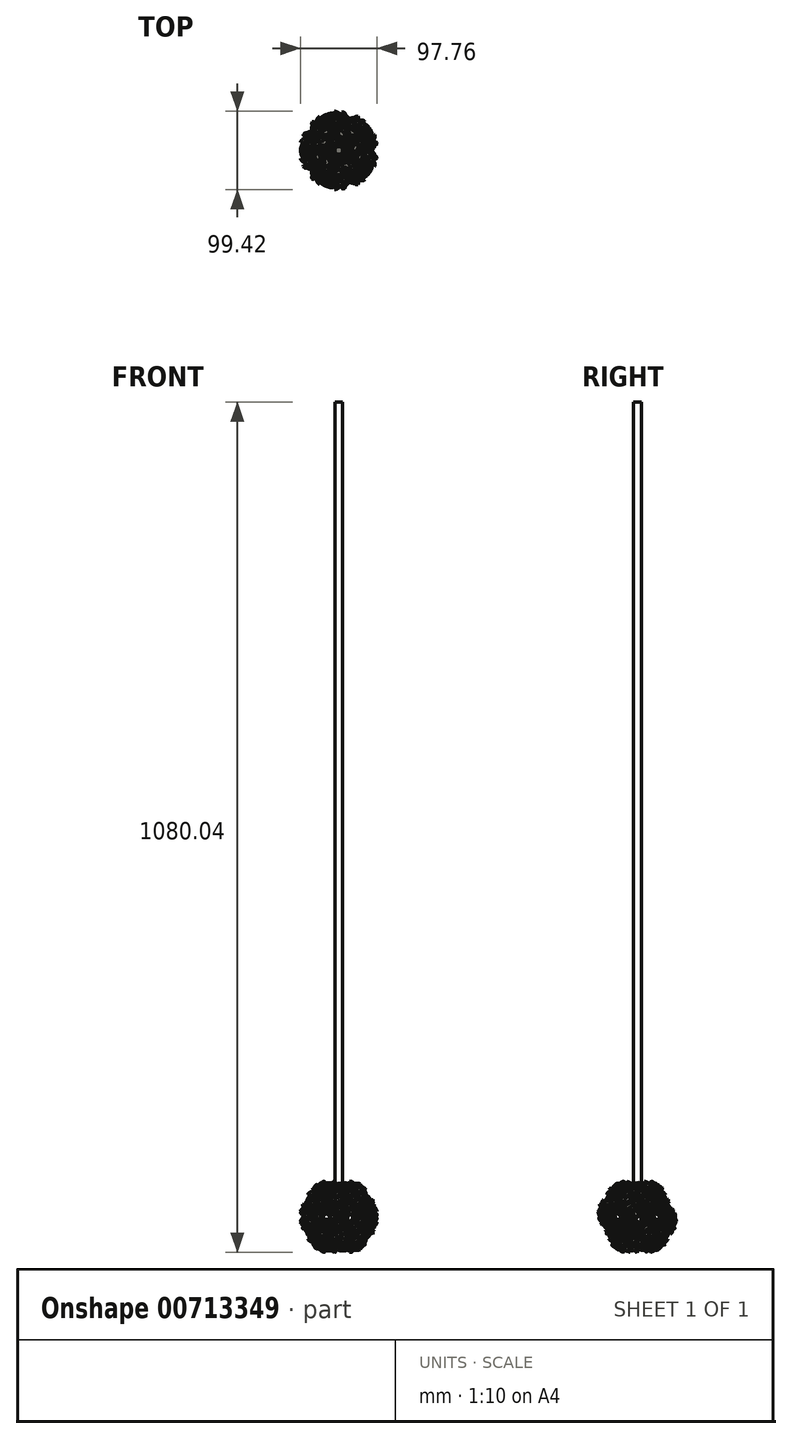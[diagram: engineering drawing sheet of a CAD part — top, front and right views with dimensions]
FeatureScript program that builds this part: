
annotation { "Feature Type Name" : "Feature", "Feature Type Description" : "" }
export const myFeature = defineFeature(function(context is Context, id is Id, definition is map)
    precondition{}
    {
        {
            var Q0;
            Q0=qCreatedBy(makeId("Top.planeOp"),FACE);
            var sketch = newSketch(context, id + "F0", { "sketchPlane" : qUnion([Q0])});
            skCircle(sketch, "E0.cCircle", {"center": v(0, 0) * mm, "radius": 10.32 * mm, "construction": true});
            skLineSegment(sketch, "E0.0", {"start": v(7.5, -10.32) * mm, "end": v(-7.5, -10.32) * mm});
            skLineSegment(sketch, "E0.1", {"start": v(-7.5, -10.32) * mm, "end": v(-12.14, 3.94) * mm});
            skLineSegment(sketch, "E0.2", {"start": v(-12.14, 3.94) * mm, "end": v(0, 12.76) * mm});
            skLineSegment(sketch, "E0.3", {"start": v(0, 12.76) * mm, "end": v(12.14, 3.94) * mm});
            skLineSegment(sketch, "E0.4", {"start": v(12.14, 3.94) * mm, "end": v(7.5, -10.32) * mm});
            skPoint(sketch, "E0.0.midPoint", {"position": v(0, -10.32) * mm});
            skLineSegment(sketch, "E1", {"start": v(0, 12.76) * mm, "end": v(0, -10.32) * mm});
            skSolve(sketch);
        }
        {
            var Q0;
            Q0=qCreatedBy(makeId("Top.planeOp"),FACE);
            var sketch = newSketch(context, id + "F1", { "sketchPlane" : qUnion([Q0])});
            skCircle(sketch, "E2.cCircle", {"center": v(22.17, -7.2) * mm, "radius": 13 * mm, "construction": true});
            skLineSegment(sketch, "E2.0", {"start": v(36.84, -4.09) * mm, "end": v(32.2, -18.35) * mm});
            skLineSegment(sketch, "E2.1", {"start": v(32.2, -18.35) * mm, "end": v(17.54, -21.47) * mm});
            skLineSegment(sketch, "E2.2", {"start": v(17.54, -21.47) * mm, "end": v(7.5, -10.32) * mm});
            skLineSegment(sketch, "E2.3", {"start": v(7.5, -10.32) * mm, "end": v(12.14, 3.94) * mm});
            skLineSegment(sketch, "E2.4", {"start": v(12.14, 3.94) * mm, "end": v(26.8, 7.06) * mm});
            skLineSegment(sketch, "E2.5", {"start": v(26.8, 7.06) * mm, "end": v(36.84, -4.09) * mm});
            skPoint(sketch, "E2.0.midPoint", {"position": v(34.53, -11.22) * mm});
            skSolve(sketch);
        }
        {
            var Q0;
            Q0=makeQuery(id+"F0.imprint","IMPRINT",FACE,{"disambiguationData":[TD([[makeQuery(id+"F0.imprint","IMPRINT",EDGE,{"derivedFrom":sQuery(id+"F0.wireOp",EDGE,"E0.0")}),-1.0]])]});
            extrude(context, id + "F2", {"entities" : qUnion([Q0]), "oppositeDirection" : true, "depth" : 1 * mm});
        }
        {
            var Q0;
            Q0=makeQuery(id+"F1.imprint","IMPRINT",FACE,{"disambiguationData":[TD([[makeQuery(id+"F1.imprint","IMPRINT",EDGE,{"derivedFrom":sQuery(id+"F1.wireOp",EDGE,"E2.0")}),-1.0]])]});
            extrude(context, id + "F3", {"entities" : qUnion([Q0]), "oppositeDirection" : true, "depth" : 1 * mm});
        }
        {
            var Q0;
            Q0=makeQuery(id+"F3.opExtrude","SWEPT_BODY",BODY,{"disambiguationData":[OSD([sQuery(id+"F1.wireOp",EDGE,"E2.0"),sQuery(id+"F1.wireOp",EDGE,"E2.1"),sQuery(id+"F1.wireOp",EDGE,"E2.2"),sQuery(id+"F1.wireOp",EDGE,"E2.3"),sQuery(id+"F1.wireOp",EDGE,"E2.4"),sQuery(id+"F1.wireOp",EDGE,"E2.5")])]});
            var Q1;
            Q1=makeQuery(id+"F2.opExtrude","CAP_EDGE",EDGE,{"disambiguationData":[OSD([sQuery(id+"F0.wireOp",EDGE,"E0.4")])],"isStart":true});
            transform(context, id + "F4", {"entities" : qUnion([Q0]), "transformType" : TransformType.ROTATION, "transformAxis" : qUnion([Q1]), "angle" : 37.38 * degree, "oppositeDirection" : true, "makeCopy" : false});
        }
        {
            var Q0;
            Q0=qCreatedBy(makeId("Right.planeOp"),FACE);
            var sketch = newSketch(context, id + "F5", { "sketchPlane" : qUnion([Q0])});
            skLineSegment(sketch, "E3", {"start": v(0, 0) * mm, "end": v(0, 7.73) * mm});
            skSolve(sketch);
        }
        {
            var Q0;
            Q0=makeQuery(id+"F3.opExtrude","SWEPT_BODY",BODY,{"disambiguationData":[OSD([sQuery(id+"F1.wireOp",EDGE,"E2.0"),sQuery(id+"F1.wireOp",EDGE,"E2.1"),sQuery(id+"F1.wireOp",EDGE,"E2.2"),sQuery(id+"F1.wireOp",EDGE,"E2.3"),sQuery(id+"F1.wireOp",EDGE,"E2.4"),sQuery(id+"F1.wireOp",EDGE,"E2.5")])]});
            var Q1;
            Q1=sQuery(id+"F5.wireOp",EDGE,"E3");
            circularPattern(context, id + "F6", {"entities" : qUnion([Q0]), "axis" : qUnion([Q1]), "angle" : 72 * degree, "instanceCount" : round(5)});
        }
        {
            var Q0;
            Q0=makeQuery(id+"F6.opPattern","COPY",FACE,{"derivedFrom":makeQuery(id+"F3.opExtrude","CAP_FACE",FACE,{"disambiguationData":[OSD([sQuery(id+"F1.wireOp",EDGE,"E2.0"),sQuery(id+"F1.wireOp",EDGE,"E2.1"),sQuery(id+"F1.wireOp",EDGE,"E2.2"),sQuery(id+"F1.wireOp",EDGE,"E2.3"),sQuery(id+"F1.wireOp",EDGE,"E2.4"),sQuery(id+"F1.wireOp",EDGE,"E2.5")])],"isStart":true}),"instanceName":"4"});
            var sketch = newSketch(context, id + "F7", { "sketchPlane" : qUnion([Q0])});
            skLineSegment(sketch, "E4", {"start": v(0, -34.18) * mm, "end": v(0, -8.2) * mm});
            skLineSegment(sketch, "E5", {"start": v(-15, -21.2) * mm, "end": v(15, -21.2) * mm});
            skCircle(sketch, "E6", {"center": v(0, -21.2) * mm, "radius": 3.24 * mm});
            skSolve(sketch);
        }
        {
            var Q0;
            Q0=qCreatedBy(makeId("Right.planeOp"),FACE);
            var sketch = newSketch(context, id + "F8", { "sketchPlane" : qUnion([Q0])});
            skArc(sketch, "E7.0", {"start": v(-1.37, 0) * mm, "mid": v(-18.04, 14.75) * mm, "end": v(-20.04, -7.42) * mm});
            skLineSegment(sketch, "E8", {"start": v(-20.04, -7.42) * mm, "end": v(-24.47, -10.8) * mm});
            skLineSegment(sketch, "E9", {"start": v(-1.37, 0) * mm, "end": v(0, 0) * mm});
            skArc(sketch, "E10", {"start": v(1.07, 1.27) * mm, "mid": v(3.46, 7.37) * mm, "end": v(2.5, 13.85) * mm});
            skArc(sketch, "E11", {"start": v(-0.8, 8.97) * mm, "mid": v(1.84, 10.74) * mm, "end": v(2.5, 13.85) * mm});
            skArc(sketch, "E12.1.0", {"start": v(-0.8, 8.97) * mm, "mid": v(-2.13, 15.94) * mm, "end": v(-6.98, 21.1) * mm});
            skArc(sketch, "E12.1.1", {"start": v(-6.75, 15.32) * mm, "mid": v(-5.72, 18.26) * mm, "end": v(-6.98, 21.1) * mm});
            skArc(sketch, "E12.2.0", {"start": v(-6.75, 15.32) * mm, "mid": v(-11.92, 20.18) * mm, "end": v(-18.89, 21.5) * mm});
            skArc(sketch, "E12.2.1", {"start": v(-15.3, 16.96) * mm, "mid": v(-16.2, 19.94) * mm, "end": v(-18.89, 21.5) * mm});
            skArc(sketch, "E12.3.0", {"start": v(-15.3, 16.96) * mm, "mid": v(-22.34, 17.85) * mm, "end": v(-28.75, 14.83) * mm});
            skArc(sketch, "E12.3.1", {"start": v(-23.18, 13.26) * mm, "mid": v(-25.66, 15.15) * mm, "end": v(-28.75, 14.83) * mm});
            skArc(sketch, "E12.4.0", {"start": v(-23.18, 13.26) * mm, "mid": v(-29.4, 9.84) * mm, "end": v(-32.81, 3.63) * mm});
            skArc(sketch, "E12.4.1", {"start": v(-27.38, 5.64) * mm, "mid": v(-30.5, 5.7) * mm, "end": v(-32.81, 3.63) * mm});
            skArc(sketch, "E12.5.0", {"start": v(-27.38, 5.64) * mm, "mid": v(-30.4, -0.78) * mm, "end": v(-29.51, -7.81) * mm});
            skArc(sketch, "E12.5.1", {"start": v(-26.3, -3) * mm, "mid": v(-28.86, -4.77) * mm, "end": v(-29.51, -7.81) * mm});
            skArc(sketch, "E12.6.0", {"start": v(-26.3, -3) * mm, "mid": v(-26.03, -7.06) * mm, "end": v(-24.49, -10.82) * mm});
            skArc(sketch, "E13", {"start": v(-24.49, -10.82) * mm, "mid": v(-20.56, -11.35) * mm, "end": v(-20.04, -7.42) * mm});
            skArc(sketch, "E14", {"start": v(-1.37, 0) * mm, "mid": v(1.27, -2.11) * mm, "end": v(1.07, 1.27) * mm});
            skSolve(sketch);
        }
        {
            var Q0;
            {var subQ2=sQuery(id+"F8.wireOp",EDGE,"E7.0");Q0=makeQuery(id+"F8.imprint","IMPRINT",FACE,{"disambiguationData":[TD([[makeQuery(id+"F8.imprint","IMPRINT",EDGE,{"derivedFrom":subQ2}),-1.0]])]});}
            extrude(context, id + "F9", {"entities" : qUnion([Q0]), "oppositeDirection" : true, "depth" : 2 * mm});
        }
        {
            var Q0;
            Q0=makeQuery(id+"F9.opExtrude","SWEPT_EDGE",EDGE,{"disambiguationData":[OSD([sQuery(id+"F8.wireOp",EDGE,"E10"),sQuery(id+"F8.wireOp",EDGE,"E14")])]});
            fillet(context, id + "F10", {"entities" : qUnion([Q0]), "radius" : 5 * mm, "tangentPropagation" : true, "allowEdgeOverflow" : false});
        }
        {
            var Q0;
            Q0=qCreatedBy(makeId("Right.planeOp"),FACE);
            var sketch = newSketch(context, id + "F11", { "sketchPlane" : qUnion([Q0])});
            skLineSegment(sketch, "E15", {"start": v(0, 0) * mm, "end": v(-20.65, -7.89) * mm});
            skLineSegment(sketch, "E16", {"start": v(0, 0) * mm, "end": v(0, 28.42) * mm});
            skSolve(sketch);
        }
        {
            var Q0;
            Q0=makeQuery(id+"F9.opExtrude","SWEPT_BODY",BODY,{"disambiguationData":[OSD([sQuery(id+"F8.wireOp",EDGE,"003f2e54-bd62-4f0b-a98e-8c36e71e2cf6"),sQuery(id+"F8.wireOp",EDGE,"8c729305-40a1-49fa-b790-4b99a3909bb6"),sQuery(id+"F8.wireOp",EDGE,"862a2a8f-3db7-4421-9c69-6ab2f53c4c24.1.0"),sQuery(id+"F8.wireOp",EDGE,"862a2a8f-3db7-4421-9c69-6ab2f53c4c24.1.1"),sQuery(id+"F8.wireOp",EDGE,"862a2a8f-3db7-4421-9c69-6ab2f53c4c24.2.0"),sQuery(id+"F8.wireOp",EDGE,"862a2a8f-3db7-4421-9c69-6ab2f53c4c24.2.1"),sQuery(id+"F8.wireOp",EDGE,"862a2a8f-3db7-4421-9c69-6ab2f53c4c24.3.0"),sQuery(id+"F8.wireOp",EDGE,"862a2a8f-3db7-4421-9c69-6ab2f53c4c24.3.1"),sQuery(id+"F8.wireOp",EDGE,"862a2a8f-3db7-4421-9c69-6ab2f53c4c24.4.0"),sQuery(id+"F8.wireOp",EDGE,"862a2a8f-3db7-4421-9c69-6ab2f53c4c24.4.1"),sQuery(id+"F8.wireOp",EDGE,"862a2a8f-3db7-4421-9c69-6ab2f53c4c24.5.0"),sQuery(id+"F8.wireOp",EDGE,"E7.0"),sQuery(id+"F8.wireOp",EDGE,"E8"),sQuery(id+"F8.wireOp",EDGE,"E9")])]});
            var Q1;
            Q1=sQuery(id+"F11.wireOp",EDGE,"E15");
            transform(context, id + "F12", {"entities" : qUnion([Q0]), "transformType" : TransformType.ROTATION, "transformAxis" : qUnion([Q1]), "angle" : 65 * degree, "makeCopy" : false});
        }
        {
            var Q0;
            Q0=makeQuery(id+"F9.opExtrude","SWEPT_BODY",BODY,{"disambiguationData":[OSD([sQuery(id+"F8.wireOp",EDGE,"003f2e54-bd62-4f0b-a98e-8c36e71e2cf6"),sQuery(id+"F8.wireOp",EDGE,"8c729305-40a1-49fa-b790-4b99a3909bb6"),sQuery(id+"F8.wireOp",EDGE,"862a2a8f-3db7-4421-9c69-6ab2f53c4c24.1.0"),sQuery(id+"F8.wireOp",EDGE,"862a2a8f-3db7-4421-9c69-6ab2f53c4c24.1.1"),sQuery(id+"F8.wireOp",EDGE,"862a2a8f-3db7-4421-9c69-6ab2f53c4c24.2.0"),sQuery(id+"F8.wireOp",EDGE,"862a2a8f-3db7-4421-9c69-6ab2f53c4c24.2.1"),sQuery(id+"F8.wireOp",EDGE,"862a2a8f-3db7-4421-9c69-6ab2f53c4c24.3.0"),sQuery(id+"F8.wireOp",EDGE,"862a2a8f-3db7-4421-9c69-6ab2f53c4c24.3.1"),sQuery(id+"F8.wireOp",EDGE,"862a2a8f-3db7-4421-9c69-6ab2f53c4c24.4.0"),sQuery(id+"F8.wireOp",EDGE,"862a2a8f-3db7-4421-9c69-6ab2f53c4c24.4.1"),sQuery(id+"F8.wireOp",EDGE,"862a2a8f-3db7-4421-9c69-6ab2f53c4c24.5.0"),sQuery(id+"F8.wireOp",EDGE,"E7.0"),sQuery(id+"F8.wireOp",EDGE,"E8"),sQuery(id+"F8.wireOp",EDGE,"E9")])]});
            var Q1;
            Q1=sQuery(id+"F11.wireOp",EDGE,"E16");
            circularPattern(context, id + "F13", {"entities" : qUnion([Q0]), "axis" : qUnion([Q1]), "angle" : 72 * degree, "instanceCount" : round(5)});
        }
        {
            var Q0;
            Q0=qCreatedBy(makeId("Right.planeOp"),FACE);
            var sketch = newSketch(context, id + "F14", { "sketchPlane" : qUnion([Q0])});
            skLineSegment(sketch, "E17.0", {"start": v(-30.97, -15.77) * mm, "end": v(-10.32, 0) * mm});
            skLineSegment(sketch, "E18", {"start": v(-20.65, -7.89) * mm, "end": v(-30.05, 4.42) * mm});
            skSolve(sketch);
        }
        {
            var Q0;
            Q0=makeQuery(id+"F9.opExtrude","SWEPT_BODY",BODY,{"disambiguationData":[OSD([sQuery(id+"F8.wireOp",EDGE,"003f2e54-bd62-4f0b-a98e-8c36e71e2cf6"),sQuery(id+"F8.wireOp",EDGE,"8c729305-40a1-49fa-b790-4b99a3909bb6"),sQuery(id+"F8.wireOp",EDGE,"862a2a8f-3db7-4421-9c69-6ab2f53c4c24.1.0"),sQuery(id+"F8.wireOp",EDGE,"862a2a8f-3db7-4421-9c69-6ab2f53c4c24.1.1"),sQuery(id+"F8.wireOp",EDGE,"862a2a8f-3db7-4421-9c69-6ab2f53c4c24.2.0"),sQuery(id+"F8.wireOp",EDGE,"862a2a8f-3db7-4421-9c69-6ab2f53c4c24.2.1"),sQuery(id+"F8.wireOp",EDGE,"862a2a8f-3db7-4421-9c69-6ab2f53c4c24.3.0"),sQuery(id+"F8.wireOp",EDGE,"862a2a8f-3db7-4421-9c69-6ab2f53c4c24.3.1"),sQuery(id+"F8.wireOp",EDGE,"862a2a8f-3db7-4421-9c69-6ab2f53c4c24.4.0"),sQuery(id+"F8.wireOp",EDGE,"862a2a8f-3db7-4421-9c69-6ab2f53c4c24.4.1"),sQuery(id+"F8.wireOp",EDGE,"862a2a8f-3db7-4421-9c69-6ab2f53c4c24.5.0"),sQuery(id+"F8.wireOp",EDGE,"E7.0"),sQuery(id+"F8.wireOp",EDGE,"E8"),sQuery(id+"F8.wireOp",EDGE,"E9")])]});
            var Q1;
            Q1=sQuery(id+"F14.wireOp",EDGE,"E18");
            circularPattern(context, id + "F15", {"entities" : qUnion([Q0]), "axis" : qUnion([Q1]), "angle" : 120 * degree, "instanceCount" : round(3)});
        }
        {
            var Q0;
            Q0=makeQuery(id+"F15.opPattern","COPY",BODY,{"derivedFrom":makeQuery(id+"F9.opExtrude","SWEPT_BODY",BODY,{"disambiguationData":[OSD([sQuery(id+"F8.wireOp",EDGE,"E7.0"),sQuery(id+"F8.wireOp",EDGE,"E10"),sQuery(id+"F8.wireOp",EDGE,"E11"),sQuery(id+"F8.wireOp",EDGE,"E12.1.0"),sQuery(id+"F8.wireOp",EDGE,"E12.1.1"),sQuery(id+"F8.wireOp",EDGE,"E12.2.0"),sQuery(id+"F8.wireOp",EDGE,"E12.2.1"),sQuery(id+"F8.wireOp",EDGE,"E12.3.0"),sQuery(id+"F8.wireOp",EDGE,"E12.3.1"),sQuery(id+"F8.wireOp",EDGE,"E12.4.0"),sQuery(id+"F8.wireOp",EDGE,"E12.4.1"),sQuery(id+"F8.wireOp",EDGE,"E12.5.0"),sQuery(id+"F8.wireOp",EDGE,"E12.5.1"),sQuery(id+"F8.wireOp",EDGE,"E12.6.0"),sQuery(id+"F8.wireOp",EDGE,"E13"),sQuery(id+"F8.wireOp",EDGE,"E14")])]}),"instanceName":"2"});
            var Q1;
            Q1=makeQuery(id+"F15.opPattern","COPY",BODY,{"derivedFrom":makeQuery(id+"F9.opExtrude","SWEPT_BODY",BODY,{"disambiguationData":[OSD([sQuery(id+"F8.wireOp",EDGE,"E7.0"),sQuery(id+"F8.wireOp",EDGE,"E10"),sQuery(id+"F8.wireOp",EDGE,"E11"),sQuery(id+"F8.wireOp",EDGE,"E12.1.0"),sQuery(id+"F8.wireOp",EDGE,"E12.1.1"),sQuery(id+"F8.wireOp",EDGE,"E12.2.0"),sQuery(id+"F8.wireOp",EDGE,"E12.2.1"),sQuery(id+"F8.wireOp",EDGE,"E12.3.0"),sQuery(id+"F8.wireOp",EDGE,"E12.3.1"),sQuery(id+"F8.wireOp",EDGE,"E12.4.0"),sQuery(id+"F8.wireOp",EDGE,"E12.4.1"),sQuery(id+"F8.wireOp",EDGE,"E12.5.0"),sQuery(id+"F8.wireOp",EDGE,"E12.5.1"),sQuery(id+"F8.wireOp",EDGE,"E12.6.0"),sQuery(id+"F8.wireOp",EDGE,"E13"),sQuery(id+"F8.wireOp",EDGE,"E14")])]}),"instanceName":"1"});
            var Q2;
            Q2=sQuery(id+"F11.wireOp",EDGE,"E16");
            circularPattern(context, id + "F16", {"entities" : qUnion([Q0, Q1]), "axis" : qUnion([Q2]), "angle" : 72 * degree, "instanceCount" : round(5)});
        }
        {
            var Q0;
            Q0=makeQuery(id+"F3.opExtrude","SWEPT_BODY",BODY,{"disambiguationData":[OSD([sQuery(id+"F1.wireOp",EDGE,"E2.0"),sQuery(id+"F1.wireOp",EDGE,"E2.1"),sQuery(id+"F1.wireOp",EDGE,"E2.2"),sQuery(id+"F1.wireOp",EDGE,"E2.3"),sQuery(id+"F1.wireOp",EDGE,"E2.4"),sQuery(id+"F1.wireOp",EDGE,"E2.5")])]});
            var Q1;
            Q1=makeQuery(id+"F16.opPattern","COPY",BODY,{"derivedFrom":makeQuery(id+"F15.opPattern","COPY",BODY,{"derivedFrom":makeQuery(id+"F9.opExtrude","SWEPT_BODY",BODY,{"disambiguationData":[OSD([sQuery(id+"F8.wireOp",EDGE,"E7.0"),sQuery(id+"F8.wireOp",EDGE,"E10"),sQuery(id+"F8.wireOp",EDGE,"E11"),sQuery(id+"F8.wireOp",EDGE,"E12.1.0"),sQuery(id+"F8.wireOp",EDGE,"E12.1.1"),sQuery(id+"F8.wireOp",EDGE,"E12.2.0"),sQuery(id+"F8.wireOp",EDGE,"E12.2.1"),sQuery(id+"F8.wireOp",EDGE,"E12.3.0"),sQuery(id+"F8.wireOp",EDGE,"E12.3.1"),sQuery(id+"F8.wireOp",EDGE,"E12.4.0"),sQuery(id+"F8.wireOp",EDGE,"E12.4.1"),sQuery(id+"F8.wireOp",EDGE,"E12.5.0"),sQuery(id+"F8.wireOp",EDGE,"E12.5.1"),sQuery(id+"F8.wireOp",EDGE,"E12.6.0"),sQuery(id+"F8.wireOp",EDGE,"E13"),sQuery(id+"F8.wireOp",EDGE,"E14")])]}),"instanceName":"1"}),"instanceName":"1"});
            var Q2;
            Q2=makeQuery(id+"F13.opPattern","COPY",BODY,{"derivedFrom":makeQuery(id+"F9.opExtrude","SWEPT_BODY",BODY,{"disambiguationData":[OSD([sQuery(id+"F8.wireOp",EDGE,"E7.0"),sQuery(id+"F8.wireOp",EDGE,"E10"),sQuery(id+"F8.wireOp",EDGE,"E11"),sQuery(id+"F8.wireOp",EDGE,"E12.1.0"),sQuery(id+"F8.wireOp",EDGE,"E12.1.1"),sQuery(id+"F8.wireOp",EDGE,"E12.2.0"),sQuery(id+"F8.wireOp",EDGE,"E12.2.1"),sQuery(id+"F8.wireOp",EDGE,"E12.3.0"),sQuery(id+"F8.wireOp",EDGE,"E12.3.1"),sQuery(id+"F8.wireOp",EDGE,"E12.4.0"),sQuery(id+"F8.wireOp",EDGE,"E12.4.1"),sQuery(id+"F8.wireOp",EDGE,"E12.5.0"),sQuery(id+"F8.wireOp",EDGE,"E12.5.1"),sQuery(id+"F8.wireOp",EDGE,"E12.6.0"),sQuery(id+"F8.wireOp",EDGE,"E13"),sQuery(id+"F8.wireOp",EDGE,"E14")])]}),"instanceName":"1"});
            var Q3;
            Q3=makeQuery(id+"F16.opPattern","COPY",BODY,{"derivedFrom":makeQuery(id+"F15.opPattern","COPY",BODY,{"derivedFrom":makeQuery(id+"F9.opExtrude","SWEPT_BODY",BODY,{"disambiguationData":[OSD([sQuery(id+"F8.wireOp",EDGE,"E7.0"),sQuery(id+"F8.wireOp",EDGE,"E10"),sQuery(id+"F8.wireOp",EDGE,"E11"),sQuery(id+"F8.wireOp",EDGE,"E12.1.0"),sQuery(id+"F8.wireOp",EDGE,"E12.1.1"),sQuery(id+"F8.wireOp",EDGE,"E12.2.0"),sQuery(id+"F8.wireOp",EDGE,"E12.2.1"),sQuery(id+"F8.wireOp",EDGE,"E12.3.0"),sQuery(id+"F8.wireOp",EDGE,"E12.3.1"),sQuery(id+"F8.wireOp",EDGE,"E12.4.0"),sQuery(id+"F8.wireOp",EDGE,"E12.4.1"),sQuery(id+"F8.wireOp",EDGE,"E12.5.0"),sQuery(id+"F8.wireOp",EDGE,"E12.5.1"),sQuery(id+"F8.wireOp",EDGE,"E12.6.0"),sQuery(id+"F8.wireOp",EDGE,"E13"),sQuery(id+"F8.wireOp",EDGE,"E14")])]}),"instanceName":"2"}),"instanceName":"1"});
            var Q4;
            Q4=sQuery(id+"F14.wireOp",EDGE,"E18");
            circularPattern(context, id + "F17", {"entities" : qUnion([Q0, Q1, Q2, Q3]), "axis" : qUnion([Q4]), "angle" : 120 * degree, "instanceCount" : 2, "oppositeDirection" : true});
        }
        {
            var Q0;
            Q0=makeQuery(id+"F2.opExtrude","SWEPT_BODY",BODY,{"disambiguationData":[OSD([sQuery(id+"F0.wireOp",EDGE,"E0.0"),sQuery(id+"F0.wireOp",EDGE,"E0.1"),sQuery(id+"F0.wireOp",EDGE,"E0.2"),sQuery(id+"F0.wireOp",EDGE,"E0.3"),sQuery(id+"F0.wireOp",EDGE,"E0.4")])]});
            var Q1;
            Q1=makeQuery(id+"F13.opPattern","COPY",BODY,{"derivedFrom":makeQuery(id+"F9.opExtrude","SWEPT_BODY",BODY,{"disambiguationData":[OSD([sQuery(id+"F8.wireOp",EDGE,"E7.0"),sQuery(id+"F8.wireOp",EDGE,"E10"),sQuery(id+"F8.wireOp",EDGE,"E11"),sQuery(id+"F8.wireOp",EDGE,"E12.1.0"),sQuery(id+"F8.wireOp",EDGE,"E12.1.1"),sQuery(id+"F8.wireOp",EDGE,"E12.2.0"),sQuery(id+"F8.wireOp",EDGE,"E12.2.1"),sQuery(id+"F8.wireOp",EDGE,"E12.3.0"),sQuery(id+"F8.wireOp",EDGE,"E12.3.1"),sQuery(id+"F8.wireOp",EDGE,"E12.4.0"),sQuery(id+"F8.wireOp",EDGE,"E12.4.1"),sQuery(id+"F8.wireOp",EDGE,"E12.5.0"),sQuery(id+"F8.wireOp",EDGE,"E12.5.1"),sQuery(id+"F8.wireOp",EDGE,"E12.6.0"),sQuery(id+"F8.wireOp",EDGE,"E13"),sQuery(id+"F8.wireOp",EDGE,"E14")])]}),"instanceName":"2"});
            var Q2;
            Q2=makeQuery(id+"F13.opPattern","COPY",BODY,{"derivedFrom":makeQuery(id+"F9.opExtrude","SWEPT_BODY",BODY,{"disambiguationData":[OSD([sQuery(id+"F8.wireOp",EDGE,"E7.0"),sQuery(id+"F8.wireOp",EDGE,"E10"),sQuery(id+"F8.wireOp",EDGE,"E11"),sQuery(id+"F8.wireOp",EDGE,"E12.1.0"),sQuery(id+"F8.wireOp",EDGE,"E12.1.1"),sQuery(id+"F8.wireOp",EDGE,"E12.2.0"),sQuery(id+"F8.wireOp",EDGE,"E12.2.1"),sQuery(id+"F8.wireOp",EDGE,"E12.3.0"),sQuery(id+"F8.wireOp",EDGE,"E12.3.1"),sQuery(id+"F8.wireOp",EDGE,"E12.4.0"),sQuery(id+"F8.wireOp",EDGE,"E12.4.1"),sQuery(id+"F8.wireOp",EDGE,"E12.5.0"),sQuery(id+"F8.wireOp",EDGE,"E12.5.1"),sQuery(id+"F8.wireOp",EDGE,"E12.6.0"),sQuery(id+"F8.wireOp",EDGE,"E13"),sQuery(id+"F8.wireOp",EDGE,"E14")])]}),"instanceName":"3"});
            var Q3;
            Q3=sQuery(id+"F14.wireOp",EDGE,"E18");
            circularPattern(context, id + "F18", {"entities" : qUnion([Q0, Q1, Q2]), "axis" : qUnion([Q3]), "angle" : 120 * degree, "instanceCount" : round(3)});
        }
        {
            var Q0;
            Q0=makeQuery(id+"F18.opPattern","COPY",FACE,{"derivedFrom":makeQuery(id+"F2.opExtrude","CAP_FACE",FACE,{"disambiguationData":[OSD([sQuery(id+"F0.wireOp",EDGE,"E0.0"),sQuery(id+"F0.wireOp",EDGE,"E0.1"),sQuery(id+"F0.wireOp",EDGE,"E0.2"),sQuery(id+"F0.wireOp",EDGE,"E0.3"),sQuery(id+"F0.wireOp",EDGE,"E0.4")])],"isStart":true}),"instanceName":"1"});
            var sketch = newSketch(context, id + "F19", { "sketchPlane" : qUnion([Q0])});
            skLineSegment(sketch, "E19", {"start": v(-1.3, -23.63) * mm, "end": v(-19.97, -37.2) * mm});
            skLineSegment(sketch, "E20", {"start": v(-19.97, -22.2) * mm, "end": v(-1.3, -35.77) * mm});
            skSolve(sketch);
        }
        {
            var Q0;
            Q0=sQuery(id+"F19.wireOp",VERTEX,"E19.end");
            var Q1;
            Q1=sQuery(id+"F19.wireOp",VERTEX,"E19.start");
            var Q2;
            Q2=sQuery(id+"F14.wireOp",VERTEX,"E18.end");
            cPlane(context, id + "F20", {"entities" : qUnion([Q0, Q1, Q2]), "cplaneType" : CPlaneType.THREE_POINT, "offset" : 150 * mm, "width" : 150 * mm, "height" : 150 * mm});
        }
        {
            var Q0;
            Q0=qCreatedBy(id+"F20.planeOp",FACE);
            var sketch = newSketch(context, id + "F21", { "sketchPlane" : qUnion([Q0])});
            skLineSegment(sketch, "E21.0", {"start": v(23.59, 6.27) * mm, "end": v(41.93, -7.75) * mm});
            skLineSegment(sketch, "E21.1", {"start": v(34.92, -2.4) * mm, "end": v(29.26, 1.94) * mm});
            skLineSegment(sketch, "E22", {"start": v(31.8, 0) * mm, "end": v(33.22, 1.87) * mm});
            skLineSegment(sketch, "E23", {"start": v(33.22, 1.87) * mm, "end": v(37.58, 7.58) * mm});
            skSolve(sketch);
        }
        {
            var Q0;
            Q0=makeQuery(id+"F17.opPattern","COPY",BODY,{"derivedFrom":makeQuery(id+"F3.opExtrude","SWEPT_BODY",BODY,{"disambiguationData":[OSD([sQuery(id+"F1.wireOp",EDGE,"E2.0"),sQuery(id+"F1.wireOp",EDGE,"E2.1"),sQuery(id+"F1.wireOp",EDGE,"E2.2"),sQuery(id+"F1.wireOp",EDGE,"E2.3"),sQuery(id+"F1.wireOp",EDGE,"E2.4"),sQuery(id+"F1.wireOp",EDGE,"E2.5")])]}),"instanceName":"1"});
            var Q1;
            Q1=makeQuery(id+"F17.opPattern","COPY",BODY,{"derivedFrom":makeQuery(id+"F13.opPattern","COPY",BODY,{"derivedFrom":makeQuery(id+"F9.opExtrude","SWEPT_BODY",BODY,{"disambiguationData":[OSD([sQuery(id+"F8.wireOp",EDGE,"E7.0"),sQuery(id+"F8.wireOp",EDGE,"E10"),sQuery(id+"F8.wireOp",EDGE,"E11"),sQuery(id+"F8.wireOp",EDGE,"E12.1.0"),sQuery(id+"F8.wireOp",EDGE,"E12.1.1"),sQuery(id+"F8.wireOp",EDGE,"E12.2.0"),sQuery(id+"F8.wireOp",EDGE,"E12.2.1"),sQuery(id+"F8.wireOp",EDGE,"E12.3.0"),sQuery(id+"F8.wireOp",EDGE,"E12.3.1"),sQuery(id+"F8.wireOp",EDGE,"E12.4.0"),sQuery(id+"F8.wireOp",EDGE,"E12.4.1"),sQuery(id+"F8.wireOp",EDGE,"E12.5.0"),sQuery(id+"F8.wireOp",EDGE,"E12.5.1"),sQuery(id+"F8.wireOp",EDGE,"E12.6.0"),sQuery(id+"F8.wireOp",EDGE,"E13"),sQuery(id+"F8.wireOp",EDGE,"E14")])]}),"instanceName":"1"}),"instanceName":"1"});
            var Q2;
            Q2=makeQuery(id+"F17.opPattern","COPY",BODY,{"derivedFrom":makeQuery(id+"F16.opPattern","COPY",BODY,{"derivedFrom":makeQuery(id+"F15.opPattern","COPY",BODY,{"derivedFrom":makeQuery(id+"F9.opExtrude","SWEPT_BODY",BODY,{"disambiguationData":[OSD([sQuery(id+"F8.wireOp",EDGE,"E7.0"),sQuery(id+"F8.wireOp",EDGE,"E10"),sQuery(id+"F8.wireOp",EDGE,"E11"),sQuery(id+"F8.wireOp",EDGE,"E12.1.0"),sQuery(id+"F8.wireOp",EDGE,"E12.1.1"),sQuery(id+"F8.wireOp",EDGE,"E12.2.0"),sQuery(id+"F8.wireOp",EDGE,"E12.2.1"),sQuery(id+"F8.wireOp",EDGE,"E12.3.0"),sQuery(id+"F8.wireOp",EDGE,"E12.3.1"),sQuery(id+"F8.wireOp",EDGE,"E12.4.0"),sQuery(id+"F8.wireOp",EDGE,"E12.4.1"),sQuery(id+"F8.wireOp",EDGE,"E12.5.0"),sQuery(id+"F8.wireOp",EDGE,"E12.5.1"),sQuery(id+"F8.wireOp",EDGE,"E12.6.0"),sQuery(id+"F8.wireOp",EDGE,"E13"),sQuery(id+"F8.wireOp",EDGE,"E14")])]}),"instanceName":"2"}),"instanceName":"1"}),"instanceName":"1"});
            var Q3;
            Q3=makeQuery(id+"F17.opPattern","COPY",BODY,{"derivedFrom":makeQuery(id+"F16.opPattern","COPY",BODY,{"derivedFrom":makeQuery(id+"F15.opPattern","COPY",BODY,{"derivedFrom":makeQuery(id+"F9.opExtrude","SWEPT_BODY",BODY,{"disambiguationData":[OSD([sQuery(id+"F8.wireOp",EDGE,"E7.0"),sQuery(id+"F8.wireOp",EDGE,"E10"),sQuery(id+"F8.wireOp",EDGE,"E11"),sQuery(id+"F8.wireOp",EDGE,"E12.1.0"),sQuery(id+"F8.wireOp",EDGE,"E12.1.1"),sQuery(id+"F8.wireOp",EDGE,"E12.2.0"),sQuery(id+"F8.wireOp",EDGE,"E12.2.1"),sQuery(id+"F8.wireOp",EDGE,"E12.3.0"),sQuery(id+"F8.wireOp",EDGE,"E12.3.1"),sQuery(id+"F8.wireOp",EDGE,"E12.4.0"),sQuery(id+"F8.wireOp",EDGE,"E12.4.1"),sQuery(id+"F8.wireOp",EDGE,"E12.5.0"),sQuery(id+"F8.wireOp",EDGE,"E12.5.1"),sQuery(id+"F8.wireOp",EDGE,"E12.6.0"),sQuery(id+"F8.wireOp",EDGE,"E13"),sQuery(id+"F8.wireOp",EDGE,"E14")])]}),"instanceName":"1"}),"instanceName":"1"}),"instanceName":"1"});
            var Q4;
            Q4=sQuery(id+"F21.wireOp",EDGE,"E22");
            circularPattern(context, id + "F22", {"entities" : qUnion([Q0, Q1, Q2, Q3]), "axis" : qUnion([Q4]), "angle" : 72 * degree, "instanceCount" : round(3), "oppositeDirection" : true});
        }
        {
            var Q0;
            Q0=makeQuery(id+"F18.opPattern","COPY",FACE,{"derivedFrom":makeQuery(id+"F2.opExtrude","CAP_FACE",FACE,{"disambiguationData":[OSD([sQuery(id+"F0.wireOp",EDGE,"E0.0"),sQuery(id+"F0.wireOp",EDGE,"E0.1"),sQuery(id+"F0.wireOp",EDGE,"E0.2"),sQuery(id+"F0.wireOp",EDGE,"E0.3"),sQuery(id+"F0.wireOp",EDGE,"E0.4")])],"isStart":true}),"instanceName":"2"});
            var sketch = newSketch(context, id + "F23", { "sketchPlane" : qUnion([Q0])});
            skLineSegment(sketch, "E24", {"start": v(1.3, -23.63) * mm, "end": v(19.97, -37.2) * mm});
            skLineSegment(sketch, "E25", {"start": v(5.7, -41.83) * mm, "end": v(12.84, -19.88) * mm});
            skSolve(sketch);
        }
        {
            var Q0;
            Q0=sQuery(id+"F23.wireOp",VERTEX,"E24.end");
            var Q1;
            Q1=sQuery(id+"F23.wireOp",VERTEX,"E24.start");
            var Q2;
            Q2=sQuery(id+"F14.wireOp",VERTEX,"E18.end");
            cPlane(context, id + "F24", {"entities" : qUnion([Q0, Q1, Q2]), "cplaneType" : CPlaneType.THREE_POINT, "offset" : 150 * mm, "width" : 150 * mm, "height" : 150 * mm});
        }
        {
            var Q0;
            Q0=qCreatedBy(id+"F24.planeOp",FACE);
            var sketch = newSketch(context, id + "F25", { "sketchPlane" : qUnion([Q0])});
            skLineSegment(sketch, "E26.0", {"start": v(23.59, 6.27) * mm, "end": v(41.93, -7.75) * mm});
            skLineSegment(sketch, "E26.1", {"start": v(34.92, -2.4) * mm, "end": v(29.26, 1.94) * mm});
            skLineSegment(sketch, "E27", {"start": v(31.8, 0) * mm, "end": v(36.23, 5.8) * mm});
            skSolve(sketch);
        }
        {
            var Q0;
            Q0=makeQuery(id+"F3.opExtrude","SWEPT_BODY",BODY,{"disambiguationData":[OSD([sQuery(id+"F1.wireOp",EDGE,"E2.0"),sQuery(id+"F1.wireOp",EDGE,"E2.1"),sQuery(id+"F1.wireOp",EDGE,"E2.2"),sQuery(id+"F1.wireOp",EDGE,"E2.3"),sQuery(id+"F1.wireOp",EDGE,"E2.4"),sQuery(id+"F1.wireOp",EDGE,"E2.5")])]});
            var Q1;
            Q1=makeQuery(id+"F16.opPattern","COPY",BODY,{"derivedFrom":makeQuery(id+"F15.opPattern","COPY",BODY,{"derivedFrom":makeQuery(id+"F9.opExtrude","SWEPT_BODY",BODY,{"disambiguationData":[OSD([sQuery(id+"F8.wireOp",EDGE,"E7.0"),sQuery(id+"F8.wireOp",EDGE,"E10"),sQuery(id+"F8.wireOp",EDGE,"E11"),sQuery(id+"F8.wireOp",EDGE,"E12.1.0"),sQuery(id+"F8.wireOp",EDGE,"E12.1.1"),sQuery(id+"F8.wireOp",EDGE,"E12.2.0"),sQuery(id+"F8.wireOp",EDGE,"E12.2.1"),sQuery(id+"F8.wireOp",EDGE,"E12.3.0"),sQuery(id+"F8.wireOp",EDGE,"E12.3.1"),sQuery(id+"F8.wireOp",EDGE,"E12.4.0"),sQuery(id+"F8.wireOp",EDGE,"E12.4.1"),sQuery(id+"F8.wireOp",EDGE,"E12.5.0"),sQuery(id+"F8.wireOp",EDGE,"E12.5.1"),sQuery(id+"F8.wireOp",EDGE,"E12.6.0"),sQuery(id+"F8.wireOp",EDGE,"E13"),sQuery(id+"F8.wireOp",EDGE,"E14")])]}),"instanceName":"2"}),"instanceName":"1"});
            var Q2;
            Q2=makeQuery(id+"F13.opPattern","COPY",BODY,{"derivedFrom":makeQuery(id+"F9.opExtrude","SWEPT_BODY",BODY,{"disambiguationData":[OSD([sQuery(id+"F8.wireOp",EDGE,"E7.0"),sQuery(id+"F8.wireOp",EDGE,"E10"),sQuery(id+"F8.wireOp",EDGE,"E11"),sQuery(id+"F8.wireOp",EDGE,"E12.1.0"),sQuery(id+"F8.wireOp",EDGE,"E12.1.1"),sQuery(id+"F8.wireOp",EDGE,"E12.2.0"),sQuery(id+"F8.wireOp",EDGE,"E12.2.1"),sQuery(id+"F8.wireOp",EDGE,"E12.3.0"),sQuery(id+"F8.wireOp",EDGE,"E12.3.1"),sQuery(id+"F8.wireOp",EDGE,"E12.4.0"),sQuery(id+"F8.wireOp",EDGE,"E12.4.1"),sQuery(id+"F8.wireOp",EDGE,"E12.5.0"),sQuery(id+"F8.wireOp",EDGE,"E12.5.1"),sQuery(id+"F8.wireOp",EDGE,"E12.6.0"),sQuery(id+"F8.wireOp",EDGE,"E13"),sQuery(id+"F8.wireOp",EDGE,"E14")])]}),"instanceName":"1"});
            var Q3;
            Q3=makeQuery(id+"F16.opPattern","COPY",BODY,{"derivedFrom":makeQuery(id+"F15.opPattern","COPY",BODY,{"derivedFrom":makeQuery(id+"F9.opExtrude","SWEPT_BODY",BODY,{"disambiguationData":[OSD([sQuery(id+"F8.wireOp",EDGE,"E7.0"),sQuery(id+"F8.wireOp",EDGE,"E10"),sQuery(id+"F8.wireOp",EDGE,"E11"),sQuery(id+"F8.wireOp",EDGE,"E12.1.0"),sQuery(id+"F8.wireOp",EDGE,"E12.1.1"),sQuery(id+"F8.wireOp",EDGE,"E12.2.0"),sQuery(id+"F8.wireOp",EDGE,"E12.2.1"),sQuery(id+"F8.wireOp",EDGE,"E12.3.0"),sQuery(id+"F8.wireOp",EDGE,"E12.3.1"),sQuery(id+"F8.wireOp",EDGE,"E12.4.0"),sQuery(id+"F8.wireOp",EDGE,"E12.4.1"),sQuery(id+"F8.wireOp",EDGE,"E12.5.0"),sQuery(id+"F8.wireOp",EDGE,"E12.5.1"),sQuery(id+"F8.wireOp",EDGE,"E12.6.0"),sQuery(id+"F8.wireOp",EDGE,"E13"),sQuery(id+"F8.wireOp",EDGE,"E14")])]}),"instanceName":"1"}),"instanceName":"1"});
            var Q4;
            Q4=sQuery(id+"F25.wireOp",EDGE,"E27");
            circularPattern(context, id + "F26", {"entities" : qUnion([Q0, Q1, Q2, Q3]), "axis" : qUnion([Q4]), "angle" : 72 * degree, "instanceCount" : round(3), "oppositeDirection" : true});
        }
        {
            var Q0;
            Q0=makeQuery(id+"F17.opPattern","COPY",FACE,{"derivedFrom":makeQuery(id+"F3.opExtrude","CAP_FACE",FACE,{"disambiguationData":[OSD([sQuery(id+"F1.wireOp",EDGE,"E2.0"),sQuery(id+"F1.wireOp",EDGE,"E2.1"),sQuery(id+"F1.wireOp",EDGE,"E2.2"),sQuery(id+"F1.wireOp",EDGE,"E2.3"),sQuery(id+"F1.wireOp",EDGE,"E2.4"),sQuery(id+"F1.wireOp",EDGE,"E2.5")])],"isStart":true}),"instanceName":"1"});
            var sketch = newSketch(context, id + "F27", { "sketchPlane" : qUnion([Q0])});
            skLineSegment(sketch, "E28", {"start": v(0, -47.28) * mm, "end": v(0, -21.3) * mm});
            skSolve(sketch);
        }
        {
            var Q0;
            Q0=qCreatedBy(makeId("Right.planeOp"),FACE);
            var sketch = newSketch(context, id + "F28", { "sketchPlane" : qUnion([Q0])});
            skLineSegment(sketch, "E29.0", {"start": v(-35.84, -41.3) * mm, "end": v(-30.97, -15.77) * mm});
            skLineSegment(sketch, "E30", {"start": v(-33.4, -28.53) * mm, "end": v(-47.6, -25.82) * mm});
            skSolve(sketch);
        }
        {
            var Q0;
            Q0=makeQuery(id+"F18.opPattern","COPY",BODY,{"derivedFrom":makeQuery(id+"F2.opExtrude","SWEPT_BODY",BODY,{"disambiguationData":[OSD([sQuery(id+"F0.wireOp",EDGE,"E0.0"),sQuery(id+"F0.wireOp",EDGE,"E0.1"),sQuery(id+"F0.wireOp",EDGE,"E0.2"),sQuery(id+"F0.wireOp",EDGE,"E0.3"),sQuery(id+"F0.wireOp",EDGE,"E0.4")])]}),"instanceName":"2"});
            var Q1;
            Q1=sQuery(id+"F28.wireOp",EDGE,"E30");
            circularPattern(context, id + "F29", {"entities" : qUnion([Q0]), "axis" : qUnion([Q1]), "angle" : 120 * degree, "instanceCount" : 2, "oppositeDirection" : true});
        }
        {
            var Q0;
            Q0=makeQuery(id+"F29.opPattern","COPY",FACE,{"derivedFrom":makeQuery(id+"F18.opPattern","COPY",FACE,{"derivedFrom":makeQuery(id+"F2.opExtrude","CAP_FACE",FACE,{"disambiguationData":[OSD([sQuery(id+"F0.wireOp",EDGE,"E0.0"),sQuery(id+"F0.wireOp",EDGE,"E0.1"),sQuery(id+"F0.wireOp",EDGE,"E0.2"),sQuery(id+"F0.wireOp",EDGE,"E0.3"),sQuery(id+"F0.wireOp",EDGE,"E0.4")])],"isStart":true}),"instanceName":"2"}),"instanceName":"1"});
            var sketch = newSketch(context, id + "F30", { "sketchPlane" : qUnion([Q0])});
            skLineSegment(sketch, "E31", {"start": v(0, -43.99) * mm, "end": v(0, -31.23) * mm});
            skLineSegment(sketch, "E32", {"start": v(-12.14, -35.17) * mm, "end": v(9.82, -28.04) * mm});
            skPoint(sketch, "E33.orphan", {"position": v(0, -20.9) * mm});
            skSolve(sketch);
        }
        {
            var Q0;
            Q0=qCreatedBy(makeId("Right.planeOp"),FACE);
            var sketch = newSketch(context, id + "F31", { "sketchPlane" : qUnion([Q0])});
            skLineSegment(sketch, "E34.0", {"start": v(-25.52, -61.94) * mm, "end": v(-31.23, -50.52) * mm});
            skLineSegment(sketch, "E35", {"start": v(-31.23, -50.52) * mm, "end": v(-51.07, -60.45) * mm});
            skSolve(sketch);
        }
        {
            var Q0;
            Q0=makeQuery(id+"F26.opPattern","COPY",BODY,{"derivedFrom":makeQuery(id+"F3.opExtrude","SWEPT_BODY",BODY,{"disambiguationData":[OSD([sQuery(id+"F1.wireOp",EDGE,"E2.0"),sQuery(id+"F1.wireOp",EDGE,"E2.1"),sQuery(id+"F1.wireOp",EDGE,"E2.2"),sQuery(id+"F1.wireOp",EDGE,"E2.3"),sQuery(id+"F1.wireOp",EDGE,"E2.4"),sQuery(id+"F1.wireOp",EDGE,"E2.5")])]}),"instanceName":"2"});
            var Q1;
            Q1=makeQuery(id+"F26.opPattern","COPY",BODY,{"derivedFrom":makeQuery(id+"F16.opPattern","COPY",BODY,{"derivedFrom":makeQuery(id+"F15.opPattern","COPY",BODY,{"derivedFrom":makeQuery(id+"F9.opExtrude","SWEPT_BODY",BODY,{"disambiguationData":[OSD([sQuery(id+"F8.wireOp",EDGE,"E7.0"),sQuery(id+"F8.wireOp",EDGE,"E10"),sQuery(id+"F8.wireOp",EDGE,"E11"),sQuery(id+"F8.wireOp",EDGE,"E12.1.0"),sQuery(id+"F8.wireOp",EDGE,"E12.1.1"),sQuery(id+"F8.wireOp",EDGE,"E12.2.0"),sQuery(id+"F8.wireOp",EDGE,"E12.2.1"),sQuery(id+"F8.wireOp",EDGE,"E12.3.0"),sQuery(id+"F8.wireOp",EDGE,"E12.3.1"),sQuery(id+"F8.wireOp",EDGE,"E12.4.0"),sQuery(id+"F8.wireOp",EDGE,"E12.4.1"),sQuery(id+"F8.wireOp",EDGE,"E12.5.0"),sQuery(id+"F8.wireOp",EDGE,"E12.5.1"),sQuery(id+"F8.wireOp",EDGE,"E12.6.0"),sQuery(id+"F8.wireOp",EDGE,"E13"),sQuery(id+"F8.wireOp",EDGE,"E14")])]}),"instanceName":"2"}),"instanceName":"1"}),"instanceName":"2"});
            var Q2;
            Q2=makeQuery(id+"F26.opPattern","COPY",BODY,{"derivedFrom":makeQuery(id+"F13.opPattern","COPY",BODY,{"derivedFrom":makeQuery(id+"F9.opExtrude","SWEPT_BODY",BODY,{"disambiguationData":[OSD([sQuery(id+"F8.wireOp",EDGE,"E7.0"),sQuery(id+"F8.wireOp",EDGE,"E10"),sQuery(id+"F8.wireOp",EDGE,"E11"),sQuery(id+"F8.wireOp",EDGE,"E12.1.0"),sQuery(id+"F8.wireOp",EDGE,"E12.1.1"),sQuery(id+"F8.wireOp",EDGE,"E12.2.0"),sQuery(id+"F8.wireOp",EDGE,"E12.2.1"),sQuery(id+"F8.wireOp",EDGE,"E12.3.0"),sQuery(id+"F8.wireOp",EDGE,"E12.3.1"),sQuery(id+"F8.wireOp",EDGE,"E12.4.0"),sQuery(id+"F8.wireOp",EDGE,"E12.4.1"),sQuery(id+"F8.wireOp",EDGE,"E12.5.0"),sQuery(id+"F8.wireOp",EDGE,"E12.5.1"),sQuery(id+"F8.wireOp",EDGE,"E12.6.0"),sQuery(id+"F8.wireOp",EDGE,"E13"),sQuery(id+"F8.wireOp",EDGE,"E14")])]}),"instanceName":"1"}),"instanceName":"2"});
            var Q3;
            Q3=makeQuery(id+"F18.opPattern","COPY",BODY,{"derivedFrom":makeQuery(id+"F13.opPattern","COPY",BODY,{"derivedFrom":makeQuery(id+"F9.opExtrude","SWEPT_BODY",BODY,{"disambiguationData":[OSD([sQuery(id+"F8.wireOp",EDGE,"E7.0"),sQuery(id+"F8.wireOp",EDGE,"E10"),sQuery(id+"F8.wireOp",EDGE,"E11"),sQuery(id+"F8.wireOp",EDGE,"E12.1.0"),sQuery(id+"F8.wireOp",EDGE,"E12.1.1"),sQuery(id+"F8.wireOp",EDGE,"E12.2.0"),sQuery(id+"F8.wireOp",EDGE,"E12.2.1"),sQuery(id+"F8.wireOp",EDGE,"E12.3.0"),sQuery(id+"F8.wireOp",EDGE,"E12.3.1"),sQuery(id+"F8.wireOp",EDGE,"E12.4.0"),sQuery(id+"F8.wireOp",EDGE,"E12.4.1"),sQuery(id+"F8.wireOp",EDGE,"E12.5.0"),sQuery(id+"F8.wireOp",EDGE,"E12.5.1"),sQuery(id+"F8.wireOp",EDGE,"E12.6.0"),sQuery(id+"F8.wireOp",EDGE,"E13"),sQuery(id+"F8.wireOp",EDGE,"E14")])]}),"instanceName":"2"}),"instanceName":"2"});
            var Q4;
            Q4=sQuery(id+"F31.wireOp",EDGE,"E35");
            circularPattern(context, id + "F32", {"entities" : qUnion([Q0, Q1, Q2, Q3]), "axis" : qUnion([Q4]), "angle" : 72 * degree, "instanceCount" : round(3), "oppositeDirection" : true});
        }
        {
            var Q0;
            Q0=makeQuery(id+"F6.opPattern","COPY",FACE,{"derivedFrom":makeQuery(id+"F3.opExtrude","CAP_FACE",FACE,{"disambiguationData":[OSD([sQuery(id+"F1.wireOp",EDGE,"E2.0"),sQuery(id+"F1.wireOp",EDGE,"E2.1"),sQuery(id+"F1.wireOp",EDGE,"E2.2"),sQuery(id+"F1.wireOp",EDGE,"E2.3"),sQuery(id+"F1.wireOp",EDGE,"E2.4"),sQuery(id+"F1.wireOp",EDGE,"E2.5")])],"isStart":true}),"instanceName":"2"});
            var sketch = newSketch(context, id + "F33", { "sketchPlane" : qUnion([Q0])});
            skLineSegment(sketch, "E36", {"start": v(-4.1, 7.1) * mm, "end": v(-17.1, 29.6) * mm});
            skSolve(sketch);
        }
        {
            var Q0;
            Q0=sQuery(id+"F33.wireOp",VERTEX,"E36.end");
            var Q1;
            Q1=sQuery(id+"F33.wireOp",VERTEX,"E36.start");
            var Q2;
            Q2=sQuery(id+"F11.wireOp",VERTEX,"E16.end");
            cPlane(context, id + "F34", {"entities" : qUnion([Q0, Q1, Q2]), "cplaneType" : CPlaneType.THREE_POINT, "offset" : 150 * mm, "width" : 150 * mm, "height" : 150 * mm});
        }
        {
            var Q0;
            Q0=qCreatedBy(id+"F34.planeOp",FACE);
            var sketch = newSketch(context, id + "F35", { "sketchPlane" : qUnion([Q0])});
            skLineSegment(sketch, "E37.0", {"start": v(10.32, 0) * mm, "end": v(30.97, -15.77) * mm});
            skLineSegment(sketch, "E38", {"start": v(20.65, -7.89) * mm, "end": v(38.57, 15.58) * mm});
            skSolve(sketch);
        }
        {
            var Q0;
            Q0=makeQuery(id+"F2.opExtrude","SWEPT_BODY",BODY,{"disambiguationData":[OSD([sQuery(id+"F0.wireOp",EDGE,"E0.0"),sQuery(id+"F0.wireOp",EDGE,"E0.1"),sQuery(id+"F0.wireOp",EDGE,"E0.2"),sQuery(id+"F0.wireOp",EDGE,"E0.3"),sQuery(id+"F0.wireOp",EDGE,"E0.4")])]});
            var Q1;
            Q1=sQuery(id+"F35.wireOp",EDGE,"E38");
            circularPattern(context, id + "F36", {"entities" : qUnion([Q0]), "axis" : qUnion([Q1]), "angle" : 120 * degree, "instanceCount" : round(3), "oppositeDirection" : true});
        }
        {
            var Q0;
            Q0=makeQuery(id+"F36.opPattern","COPY",FACE,{"derivedFrom":makeQuery(id+"F2.opExtrude","CAP_FACE",FACE,{"disambiguationData":[OSD([sQuery(id+"F0.wireOp",EDGE,"E0.0"),sQuery(id+"F0.wireOp",EDGE,"E0.1"),sQuery(id+"F0.wireOp",EDGE,"E0.2"),sQuery(id+"F0.wireOp",EDGE,"E0.3"),sQuery(id+"F0.wireOp",EDGE,"E0.4")])],"isStart":true}),"instanceName":"1"});
            var sketch = newSketch(context, id + "F37", { "sketchPlane" : qUnion([Q0])});
            skLineSegment(sketch, "E39", {"start": v(-4.5, -30.9) * mm, "end": v(1.45, -42.2) * mm});
            skPoint(sketch, "E40.orphan", {"position": v(-9.3, -21.76) * mm});
            skSolve(sketch);
        }
        {
            var Q0;
            Q0=sQuery(id+"F37.wireOp",VERTEX,"E39.end");
            var Q1;
            Q1=sQuery(id+"F37.wireOp",VERTEX,"E39.start");
            var Q2;
            Q2=sQuery(id+"F35.wireOp",VERTEX,"E38.end");
            cPlane(context, id + "F38", {"entities" : qUnion([Q0, Q1, Q2]), "cplaneType" : CPlaneType.THREE_POINT, "offset" : 150 * mm, "width" : 150 * mm, "height" : 150 * mm});
        }
        {
            var Q0;
            Q0=qCreatedBy(id+"F38.planeOp",FACE);
            var sketch = newSketch(context, id + "F39", { "sketchPlane" : qUnion([Q0])});
            skLineSegment(sketch, "E41.0", {"start": v(29.7, -11.34) * mm, "end": v(36.4, -22.2) * mm});
            skLineSegment(sketch, "E42", {"start": v(29.7, -11.34) * mm, "end": v(58.3, 6.33) * mm});
            skSolve(sketch);
        }
        {
            var Q0;
            Q0=makeQuery(id+"F22.opPattern","COPY",BODY,{"derivedFrom":makeQuery(id+"F17.opPattern","COPY",BODY,{"derivedFrom":makeQuery(id+"F3.opExtrude","SWEPT_BODY",BODY,{"disambiguationData":[OSD([sQuery(id+"F1.wireOp",EDGE,"E2.0"),sQuery(id+"F1.wireOp",EDGE,"E2.1"),sQuery(id+"F1.wireOp",EDGE,"E2.2"),sQuery(id+"F1.wireOp",EDGE,"E2.3"),sQuery(id+"F1.wireOp",EDGE,"E2.4"),sQuery(id+"F1.wireOp",EDGE,"E2.5")])]}),"instanceName":"1"}),"instanceName":"2"});
            var Q1;
            Q1=makeQuery(id+"F22.opPattern","COPY",BODY,{"derivedFrom":makeQuery(id+"F17.opPattern","COPY",BODY,{"derivedFrom":makeQuery(id+"F16.opPattern","COPY",BODY,{"derivedFrom":makeQuery(id+"F15.opPattern","COPY",BODY,{"derivedFrom":makeQuery(id+"F9.opExtrude","SWEPT_BODY",BODY,{"disambiguationData":[OSD([sQuery(id+"F8.wireOp",EDGE,"E7.0"),sQuery(id+"F8.wireOp",EDGE,"E10"),sQuery(id+"F8.wireOp",EDGE,"E11"),sQuery(id+"F8.wireOp",EDGE,"E12.1.0"),sQuery(id+"F8.wireOp",EDGE,"E12.1.1"),sQuery(id+"F8.wireOp",EDGE,"E12.2.0"),sQuery(id+"F8.wireOp",EDGE,"E12.2.1"),sQuery(id+"F8.wireOp",EDGE,"E12.3.0"),sQuery(id+"F8.wireOp",EDGE,"E12.3.1"),sQuery(id+"F8.wireOp",EDGE,"E12.4.0"),sQuery(id+"F8.wireOp",EDGE,"E12.4.1"),sQuery(id+"F8.wireOp",EDGE,"E12.5.0"),sQuery(id+"F8.wireOp",EDGE,"E12.5.1"),sQuery(id+"F8.wireOp",EDGE,"E12.6.0"),sQuery(id+"F8.wireOp",EDGE,"E13"),sQuery(id+"F8.wireOp",EDGE,"E14")])]}),"instanceName":"2"}),"instanceName":"1"}),"instanceName":"1"}),"instanceName":"2"});
            var Q2;
            Q2=makeQuery(id+"F22.opPattern","COPY",BODY,{"derivedFrom":makeQuery(id+"F17.opPattern","COPY",BODY,{"derivedFrom":makeQuery(id+"F13.opPattern","COPY",BODY,{"derivedFrom":makeQuery(id+"F9.opExtrude","SWEPT_BODY",BODY,{"disambiguationData":[OSD([sQuery(id+"F8.wireOp",EDGE,"E7.0"),sQuery(id+"F8.wireOp",EDGE,"E10"),sQuery(id+"F8.wireOp",EDGE,"E11"),sQuery(id+"F8.wireOp",EDGE,"E12.1.0"),sQuery(id+"F8.wireOp",EDGE,"E12.1.1"),sQuery(id+"F8.wireOp",EDGE,"E12.2.0"),sQuery(id+"F8.wireOp",EDGE,"E12.2.1"),sQuery(id+"F8.wireOp",EDGE,"E12.3.0"),sQuery(id+"F8.wireOp",EDGE,"E12.3.1"),sQuery(id+"F8.wireOp",EDGE,"E12.4.0"),sQuery(id+"F8.wireOp",EDGE,"E12.4.1"),sQuery(id+"F8.wireOp",EDGE,"E12.5.0"),sQuery(id+"F8.wireOp",EDGE,"E12.5.1"),sQuery(id+"F8.wireOp",EDGE,"E12.6.0"),sQuery(id+"F8.wireOp",EDGE,"E13"),sQuery(id+"F8.wireOp",EDGE,"E14")])]}),"instanceName":"1"}),"instanceName":"1"}),"instanceName":"2"});
            var Q3;
            Q3=makeQuery(id+"F18.opPattern","COPY",BODY,{"derivedFrom":makeQuery(id+"F13.opPattern","COPY",BODY,{"derivedFrom":makeQuery(id+"F9.opExtrude","SWEPT_BODY",BODY,{"disambiguationData":[OSD([sQuery(id+"F8.wireOp",EDGE,"E7.0"),sQuery(id+"F8.wireOp",EDGE,"E10"),sQuery(id+"F8.wireOp",EDGE,"E11"),sQuery(id+"F8.wireOp",EDGE,"E12.1.0"),sQuery(id+"F8.wireOp",EDGE,"E12.1.1"),sQuery(id+"F8.wireOp",EDGE,"E12.2.0"),sQuery(id+"F8.wireOp",EDGE,"E12.2.1"),sQuery(id+"F8.wireOp",EDGE,"E12.3.0"),sQuery(id+"F8.wireOp",EDGE,"E12.3.1"),sQuery(id+"F8.wireOp",EDGE,"E12.4.0"),sQuery(id+"F8.wireOp",EDGE,"E12.4.1"),sQuery(id+"F8.wireOp",EDGE,"E12.5.0"),sQuery(id+"F8.wireOp",EDGE,"E12.5.1"),sQuery(id+"F8.wireOp",EDGE,"E12.6.0"),sQuery(id+"F8.wireOp",EDGE,"E13"),sQuery(id+"F8.wireOp",EDGE,"E14")])]}),"instanceName":"2"}),"instanceName":"1"});
            var Q4;
            Q4=sQuery(id+"F39.wireOp",EDGE,"E42");
            circularPattern(context, id + "F40", {"entities" : qUnion([Q0, Q1, Q2, Q3]), "axis" : qUnion([Q4]), "angle" : 72 * degree, "instanceCount" : round(3), "oppositeDirection" : true});
        }
        {
            var Q0;
            Q0=makeQuery(id+"F36.opPattern","COPY",FACE,{"derivedFrom":makeQuery(id+"F2.opExtrude","CAP_FACE",FACE,{"disambiguationData":[OSD([sQuery(id+"F0.wireOp",EDGE,"E0.0"),sQuery(id+"F0.wireOp",EDGE,"E0.1"),sQuery(id+"F0.wireOp",EDGE,"E0.2"),sQuery(id+"F0.wireOp",EDGE,"E0.3"),sQuery(id+"F0.wireOp",EDGE,"E0.4")])],"isStart":true}),"instanceName":"2"});
            var sketch = newSketch(context, id + "F41", { "sketchPlane" : qUnion([Q0])});
            skLineSegment(sketch, "E43", {"start": v(0, -18.47) * mm, "end": v(0, -31.23) * mm});
            skPoint(sketch, "E44.orphan", {"position": v(0, -41.55) * mm});
            skSolve(sketch);
        }
        {
            var Q0;
            Q0=sQuery(id+"F41.wireOp",VERTEX,"E43.end");
            var Q1;
            Q1=sQuery(id+"F41.wireOp",VERTEX,"E43.start");
            var Q2;
            Q2=sQuery(id+"F11.wireOp",VERTEX,"E16.end");
            cPlane(context, id + "F42", {"entities" : qUnion([Q0, Q1, Q2]), "cplaneType" : CPlaneType.THREE_POINT, "offset" : 150 * mm, "width" : 150 * mm, "height" : 150 * mm});
        }
        {
            var Q0;
            Q0=qCreatedBy(id+"F42.planeOp",FACE);
            var sketch = newSketch(context, id + "F43", { "sketchPlane" : qUnion([Q0])});
            skLineSegment(sketch, "E45.0", {"start": v(-25.52, -7.89) * mm, "end": v(-31.23, -19.3) * mm});
            skLineSegment(sketch, "E46", {"start": v(-31.23, -19.3) * mm, "end": v(-78.41, 4.3) * mm});
            skSolve(sketch);
        }
        {
            var Q0;
            Q0=makeQuery(id+"F40.opPattern","COPY",BODY,{"derivedFrom":makeQuery(id+"F22.opPattern","COPY",BODY,{"derivedFrom":makeQuery(id+"F17.opPattern","COPY",BODY,{"derivedFrom":makeQuery(id+"F3.opExtrude","SWEPT_BODY",BODY,{"disambiguationData":[OSD([sQuery(id+"F1.wireOp",EDGE,"E2.0"),sQuery(id+"F1.wireOp",EDGE,"E2.1"),sQuery(id+"F1.wireOp",EDGE,"E2.2"),sQuery(id+"F1.wireOp",EDGE,"E2.3"),sQuery(id+"F1.wireOp",EDGE,"E2.4"),sQuery(id+"F1.wireOp",EDGE,"E2.5")])]}),"instanceName":"1"}),"instanceName":"2"}),"instanceName":"2"});
            var Q1;
            Q1=makeQuery(id+"F40.opPattern","COPY",BODY,{"derivedFrom":makeQuery(id+"F22.opPattern","COPY",BODY,{"derivedFrom":makeQuery(id+"F17.opPattern","COPY",BODY,{"derivedFrom":makeQuery(id+"F13.opPattern","COPY",BODY,{"derivedFrom":makeQuery(id+"F9.opExtrude","SWEPT_BODY",BODY,{"disambiguationData":[OSD([sQuery(id+"F8.wireOp",EDGE,"E7.0"),sQuery(id+"F8.wireOp",EDGE,"E10"),sQuery(id+"F8.wireOp",EDGE,"E11"),sQuery(id+"F8.wireOp",EDGE,"E12.1.0"),sQuery(id+"F8.wireOp",EDGE,"E12.1.1"),sQuery(id+"F8.wireOp",EDGE,"E12.2.0"),sQuery(id+"F8.wireOp",EDGE,"E12.2.1"),sQuery(id+"F8.wireOp",EDGE,"E12.3.0"),sQuery(id+"F8.wireOp",EDGE,"E12.3.1"),sQuery(id+"F8.wireOp",EDGE,"E12.4.0"),sQuery(id+"F8.wireOp",EDGE,"E12.4.1"),sQuery(id+"F8.wireOp",EDGE,"E12.5.0"),sQuery(id+"F8.wireOp",EDGE,"E12.5.1"),sQuery(id+"F8.wireOp",EDGE,"E12.6.0"),sQuery(id+"F8.wireOp",EDGE,"E13"),sQuery(id+"F8.wireOp",EDGE,"E14")])]}),"instanceName":"1"}),"instanceName":"1"}),"instanceName":"2"}),"instanceName":"2"});
            var Q2;
            Q2=makeQuery(id+"F40.opPattern","COPY",BODY,{"derivedFrom":makeQuery(id+"F18.opPattern","COPY",BODY,{"derivedFrom":makeQuery(id+"F13.opPattern","COPY",BODY,{"derivedFrom":makeQuery(id+"F9.opExtrude","SWEPT_BODY",BODY,{"disambiguationData":[OSD([sQuery(id+"F8.wireOp",EDGE,"E7.0"),sQuery(id+"F8.wireOp",EDGE,"E10"),sQuery(id+"F8.wireOp",EDGE,"E11"),sQuery(id+"F8.wireOp",EDGE,"E12.1.0"),sQuery(id+"F8.wireOp",EDGE,"E12.1.1"),sQuery(id+"F8.wireOp",EDGE,"E12.2.0"),sQuery(id+"F8.wireOp",EDGE,"E12.2.1"),sQuery(id+"F8.wireOp",EDGE,"E12.3.0"),sQuery(id+"F8.wireOp",EDGE,"E12.3.1"),sQuery(id+"F8.wireOp",EDGE,"E12.4.0"),sQuery(id+"F8.wireOp",EDGE,"E12.4.1"),sQuery(id+"F8.wireOp",EDGE,"E12.5.0"),sQuery(id+"F8.wireOp",EDGE,"E12.5.1"),sQuery(id+"F8.wireOp",EDGE,"E12.6.0"),sQuery(id+"F8.wireOp",EDGE,"E13"),sQuery(id+"F8.wireOp",EDGE,"E14")])]}),"instanceName":"2"}),"instanceName":"1"}),"instanceName":"2"});
            var Q3;
            Q3=makeQuery(id+"F40.opPattern","COPY",BODY,{"derivedFrom":makeQuery(id+"F22.opPattern","COPY",BODY,{"derivedFrom":makeQuery(id+"F17.opPattern","COPY",BODY,{"derivedFrom":makeQuery(id+"F16.opPattern","COPY",BODY,{"derivedFrom":makeQuery(id+"F15.opPattern","COPY",BODY,{"derivedFrom":makeQuery(id+"F9.opExtrude","SWEPT_BODY",BODY,{"disambiguationData":[OSD([sQuery(id+"F8.wireOp",EDGE,"E7.0"),sQuery(id+"F8.wireOp",EDGE,"E10"),sQuery(id+"F8.wireOp",EDGE,"E11"),sQuery(id+"F8.wireOp",EDGE,"E12.1.0"),sQuery(id+"F8.wireOp",EDGE,"E12.1.1"),sQuery(id+"F8.wireOp",EDGE,"E12.2.0"),sQuery(id+"F8.wireOp",EDGE,"E12.2.1"),sQuery(id+"F8.wireOp",EDGE,"E12.3.0"),sQuery(id+"F8.wireOp",EDGE,"E12.3.1"),sQuery(id+"F8.wireOp",EDGE,"E12.4.0"),sQuery(id+"F8.wireOp",EDGE,"E12.4.1"),sQuery(id+"F8.wireOp",EDGE,"E12.5.0"),sQuery(id+"F8.wireOp",EDGE,"E12.5.1"),sQuery(id+"F8.wireOp",EDGE,"E12.6.0"),sQuery(id+"F8.wireOp",EDGE,"E13"),sQuery(id+"F8.wireOp",EDGE,"E14")])]}),"instanceName":"2"}),"instanceName":"1"}),"instanceName":"1"}),"instanceName":"2"}),"instanceName":"2"});
            var Q4;
            Q4=sQuery(id+"F43.wireOp",EDGE,"E46");
            circularPattern(context, id + "F44", {"entities" : qUnion([Q0, Q1, Q2, Q3]), "axis" : qUnion([Q4]), "angle" : 72 * degree, "instanceCount" : round(3), "oppositeDirection" : true});
        }
        {
            var Q0;
            Q0=makeQuery(id+"F40.opPattern","COPY",FACE,{"derivedFrom":makeQuery(id+"F22.opPattern","COPY",FACE,{"derivedFrom":makeQuery(id+"F17.opPattern","COPY",FACE,{"derivedFrom":makeQuery(id+"F3.opExtrude","CAP_FACE",FACE,{"disambiguationData":[OSD([sQuery(id+"F1.wireOp",EDGE,"E2.0"),sQuery(id+"F1.wireOp",EDGE,"E2.1"),sQuery(id+"F1.wireOp",EDGE,"E2.2"),sQuery(id+"F1.wireOp",EDGE,"E2.3"),sQuery(id+"F1.wireOp",EDGE,"E2.4"),sQuery(id+"F1.wireOp",EDGE,"E2.5")])],"isStart":true}),"instanceName":"1"}),"instanceName":"2"}),"instanceName":"1"});
            var sketch = newSketch(context, id + "F45", { "sketchPlane" : qUnion([Q0])});
            skLineSegment(sketch, "E47", {"start": v(1.3, -21.26) * mm, "end": v(2.09, -34.23) * mm});
            skSolve(sketch);
        }
        {
            var Q0;
            Q0=sQuery(id+"F45.wireOp",VERTEX,"E47.end");
            var Q1;
            Q1=sQuery(id+"F45.wireOp",VERTEX,"E47.start");
            var Q2;
            Q2=makeQuery(id+"F6.opPattern","COPY",VERTEX,{"derivedFrom":makeQuery(id+"F3.opExtrude","CAP_VERTEX",VERTEX,{"disambiguationData":[OSD([sQuery(id+"F1.wireOp",EDGE,"E2.1"),sQuery(id+"F1.wireOp",EDGE,"E2.2")])],"isStart":true}),"instanceName":"3"});
            cPlane(context, id + "F46", {"entities" : qUnion([Q0, Q1, Q2]), "cplaneType" : CPlaneType.THREE_POINT, "offset" : 150 * mm, "width" : 150 * mm, "height" : 150 * mm});
        }
        {
            var Q0;
            Q0=qCreatedBy(id+"F46.planeOp",FACE);
            var sketch = newSketch(context, id + "F47", { "sketchPlane" : qUnion([Q0])});
            skLineSegment(sketch, "E48.0", {"start": v(-35.84, -28.53) * mm, "end": v(-33.4, -41.3) * mm});
            skLineSegment(sketch, "E49", {"start": v(-33.4, -41.3) * mm, "end": v(-61.9, -46.73) * mm});
            skSolve(sketch);
        }
        {
            var Q0;
            Q0=makeQuery(id+"F22.opPattern","COPY",BODY,{"derivedFrom":makeQuery(id+"F17.opPattern","COPY",BODY,{"derivedFrom":makeQuery(id+"F3.opExtrude","SWEPT_BODY",BODY,{"disambiguationData":[OSD([sQuery(id+"F1.wireOp",EDGE,"E2.0"),sQuery(id+"F1.wireOp",EDGE,"E2.1"),sQuery(id+"F1.wireOp",EDGE,"E2.2"),sQuery(id+"F1.wireOp",EDGE,"E2.3"),sQuery(id+"F1.wireOp",EDGE,"E2.4"),sQuery(id+"F1.wireOp",EDGE,"E2.5")])]}),"instanceName":"1"}),"instanceName":"2"});
            var Q1;
            Q1=makeQuery(id+"F22.opPattern","COPY",BODY,{"derivedFrom":makeQuery(id+"F17.opPattern","COPY",BODY,{"derivedFrom":makeQuery(id+"F13.opPattern","COPY",BODY,{"derivedFrom":makeQuery(id+"F9.opExtrude","SWEPT_BODY",BODY,{"disambiguationData":[OSD([sQuery(id+"F8.wireOp",EDGE,"E7.0"),sQuery(id+"F8.wireOp",EDGE,"E10"),sQuery(id+"F8.wireOp",EDGE,"E11"),sQuery(id+"F8.wireOp",EDGE,"E12.1.0"),sQuery(id+"F8.wireOp",EDGE,"E12.1.1"),sQuery(id+"F8.wireOp",EDGE,"E12.2.0"),sQuery(id+"F8.wireOp",EDGE,"E12.2.1"),sQuery(id+"F8.wireOp",EDGE,"E12.3.0"),sQuery(id+"F8.wireOp",EDGE,"E12.3.1"),sQuery(id+"F8.wireOp",EDGE,"E12.4.0"),sQuery(id+"F8.wireOp",EDGE,"E12.4.1"),sQuery(id+"F8.wireOp",EDGE,"E12.5.0"),sQuery(id+"F8.wireOp",EDGE,"E12.5.1"),sQuery(id+"F8.wireOp",EDGE,"E12.6.0"),sQuery(id+"F8.wireOp",EDGE,"E13"),sQuery(id+"F8.wireOp",EDGE,"E14")])]}),"instanceName":"1"}),"instanceName":"1"}),"instanceName":"2"});
            var Q2;
            Q2=makeQuery(id+"F22.opPattern","COPY",BODY,{"derivedFrom":makeQuery(id+"F17.opPattern","COPY",BODY,{"derivedFrom":makeQuery(id+"F16.opPattern","COPY",BODY,{"derivedFrom":makeQuery(id+"F15.opPattern","COPY",BODY,{"derivedFrom":makeQuery(id+"F9.opExtrude","SWEPT_BODY",BODY,{"disambiguationData":[OSD([sQuery(id+"F8.wireOp",EDGE,"E7.0"),sQuery(id+"F8.wireOp",EDGE,"E10"),sQuery(id+"F8.wireOp",EDGE,"E11"),sQuery(id+"F8.wireOp",EDGE,"E12.1.0"),sQuery(id+"F8.wireOp",EDGE,"E12.1.1"),sQuery(id+"F8.wireOp",EDGE,"E12.2.0"),sQuery(id+"F8.wireOp",EDGE,"E12.2.1"),sQuery(id+"F8.wireOp",EDGE,"E12.3.0"),sQuery(id+"F8.wireOp",EDGE,"E12.3.1"),sQuery(id+"F8.wireOp",EDGE,"E12.4.0"),sQuery(id+"F8.wireOp",EDGE,"E12.4.1"),sQuery(id+"F8.wireOp",EDGE,"E12.5.0"),sQuery(id+"F8.wireOp",EDGE,"E12.5.1"),sQuery(id+"F8.wireOp",EDGE,"E12.6.0"),sQuery(id+"F8.wireOp",EDGE,"E13"),sQuery(id+"F8.wireOp",EDGE,"E14")])]}),"instanceName":"2"}),"instanceName":"1"}),"instanceName":"1"}),"instanceName":"2"});
            var Q3;
            Q3=makeQuery(id+"F18.opPattern","COPY",BODY,{"derivedFrom":makeQuery(id+"F13.opPattern","COPY",BODY,{"derivedFrom":makeQuery(id+"F9.opExtrude","SWEPT_BODY",BODY,{"disambiguationData":[OSD([sQuery(id+"F8.wireOp",EDGE,"E7.0"),sQuery(id+"F8.wireOp",EDGE,"E10"),sQuery(id+"F8.wireOp",EDGE,"E11"),sQuery(id+"F8.wireOp",EDGE,"E12.1.0"),sQuery(id+"F8.wireOp",EDGE,"E12.1.1"),sQuery(id+"F8.wireOp",EDGE,"E12.2.0"),sQuery(id+"F8.wireOp",EDGE,"E12.2.1"),sQuery(id+"F8.wireOp",EDGE,"E12.3.0"),sQuery(id+"F8.wireOp",EDGE,"E12.3.1"),sQuery(id+"F8.wireOp",EDGE,"E12.4.0"),sQuery(id+"F8.wireOp",EDGE,"E12.4.1"),sQuery(id+"F8.wireOp",EDGE,"E12.5.0"),sQuery(id+"F8.wireOp",EDGE,"E12.5.1"),sQuery(id+"F8.wireOp",EDGE,"E12.6.0"),sQuery(id+"F8.wireOp",EDGE,"E13"),sQuery(id+"F8.wireOp",EDGE,"E14")])]}),"instanceName":"2"}),"instanceName":"1"});
            var Q4;
            Q4=sQuery(id+"F47.wireOp",EDGE,"E49");
            circularPattern(context, id + "F48", {"entities" : qUnion([Q0, Q1, Q2, Q3]), "axis" : qUnion([Q4]), "angle" : 120 * degree, "instanceCount" : 2, "oppositeDirection" : true});
        }
        {
            var Q0;
            Q0=makeQuery(id+"F26.opPattern","COPY",FACE,{"derivedFrom":makeQuery(id+"F3.opExtrude","CAP_FACE",FACE,{"disambiguationData":[OSD([sQuery(id+"F1.wireOp",EDGE,"E2.0"),sQuery(id+"F1.wireOp",EDGE,"E2.1"),sQuery(id+"F1.wireOp",EDGE,"E2.2"),sQuery(id+"F1.wireOp",EDGE,"E2.3"),sQuery(id+"F1.wireOp",EDGE,"E2.4"),sQuery(id+"F1.wireOp",EDGE,"E2.5")])],"isStart":true}),"instanceName":"1"});
            var sketch = newSketch(context, id + "F49", { "sketchPlane" : qUnion([Q0])});
            skLineSegment(sketch, "E50", {"start": v(-12.92, -27.06) * mm, "end": v(-2.09, -34.23) * mm});
            skSolve(sketch);
        }
        {
            var Q0;
            Q0=sQuery(id+"F49.wireOp",VERTEX,"E50.end");
            var Q1;
            Q1=sQuery(id+"F49.wireOp",VERTEX,"E50.start");
            var Q2;
            Q2=makeQuery(id+"F6.opPattern","COPY",VERTEX,{"derivedFrom":makeQuery(id+"F3.opExtrude","CAP_VERTEX",VERTEX,{"disambiguationData":[OSD([sQuery(id+"F1.wireOp",EDGE,"E2.0"),sQuery(id+"F1.wireOp",EDGE,"E2.5")])],"isStart":true}),"instanceName":"4"});
            cPlane(context, id + "F50", {"entities" : qUnion([Q0, Q1, Q2]), "cplaneType" : CPlaneType.THREE_POINT, "offset" : 150 * mm, "width" : 150 * mm, "height" : 150 * mm});
        }
        {
            var Q0;
            Q0=qCreatedBy(id+"F50.planeOp",FACE);
            var sketch = newSketch(context, id + "F51", { "sketchPlane" : qUnion([Q0])});
            skLineSegment(sketch, "E51.0", {"start": v(27.14, -5.92) * mm, "end": v(31.77, 6.22) * mm});
            skLineSegment(sketch, "E52", {"start": v(31.77, 6.22) * mm, "end": v(70.56, -8.6) * mm});
            skSolve(sketch);
        }
        {
            var Q0;
            Q0=makeQuery(id+"F16.opPattern","COPY",BODY,{"derivedFrom":makeQuery(id+"F15.opPattern","COPY",BODY,{"derivedFrom":makeQuery(id+"F9.opExtrude","SWEPT_BODY",BODY,{"disambiguationData":[OSD([sQuery(id+"F8.wireOp",EDGE,"E7.0"),sQuery(id+"F8.wireOp",EDGE,"E10"),sQuery(id+"F8.wireOp",EDGE,"E11"),sQuery(id+"F8.wireOp",EDGE,"E12.1.0"),sQuery(id+"F8.wireOp",EDGE,"E12.1.1"),sQuery(id+"F8.wireOp",EDGE,"E12.2.0"),sQuery(id+"F8.wireOp",EDGE,"E12.2.1"),sQuery(id+"F8.wireOp",EDGE,"E12.3.0"),sQuery(id+"F8.wireOp",EDGE,"E12.3.1"),sQuery(id+"F8.wireOp",EDGE,"E12.4.0"),sQuery(id+"F8.wireOp",EDGE,"E12.4.1"),sQuery(id+"F8.wireOp",EDGE,"E12.5.0"),sQuery(id+"F8.wireOp",EDGE,"E12.5.1"),sQuery(id+"F8.wireOp",EDGE,"E12.6.0"),sQuery(id+"F8.wireOp",EDGE,"E13"),sQuery(id+"F8.wireOp",EDGE,"E14")])]}),"instanceName":"1"}),"instanceName":"1"});
            var Q1;
            Q1=makeQuery(id+"F13.opPattern","COPY",BODY,{"derivedFrom":makeQuery(id+"F9.opExtrude","SWEPT_BODY",BODY,{"disambiguationData":[OSD([sQuery(id+"F8.wireOp",EDGE,"E7.0"),sQuery(id+"F8.wireOp",EDGE,"E10"),sQuery(id+"F8.wireOp",EDGE,"E11"),sQuery(id+"F8.wireOp",EDGE,"E12.1.0"),sQuery(id+"F8.wireOp",EDGE,"E12.1.1"),sQuery(id+"F8.wireOp",EDGE,"E12.2.0"),sQuery(id+"F8.wireOp",EDGE,"E12.2.1"),sQuery(id+"F8.wireOp",EDGE,"E12.3.0"),sQuery(id+"F8.wireOp",EDGE,"E12.3.1"),sQuery(id+"F8.wireOp",EDGE,"E12.4.0"),sQuery(id+"F8.wireOp",EDGE,"E12.4.1"),sQuery(id+"F8.wireOp",EDGE,"E12.5.0"),sQuery(id+"F8.wireOp",EDGE,"E12.5.1"),sQuery(id+"F8.wireOp",EDGE,"E12.6.0"),sQuery(id+"F8.wireOp",EDGE,"E13"),sQuery(id+"F8.wireOp",EDGE,"E14")])]}),"instanceName":"1"});
            var Q2;
            Q2=makeQuery(id+"F16.opPattern","COPY",BODY,{"derivedFrom":makeQuery(id+"F15.opPattern","COPY",BODY,{"derivedFrom":makeQuery(id+"F9.opExtrude","SWEPT_BODY",BODY,{"disambiguationData":[OSD([sQuery(id+"F8.wireOp",EDGE,"E7.0"),sQuery(id+"F8.wireOp",EDGE,"E10"),sQuery(id+"F8.wireOp",EDGE,"E11"),sQuery(id+"F8.wireOp",EDGE,"E12.1.0"),sQuery(id+"F8.wireOp",EDGE,"E12.1.1"),sQuery(id+"F8.wireOp",EDGE,"E12.2.0"),sQuery(id+"F8.wireOp",EDGE,"E12.2.1"),sQuery(id+"F8.wireOp",EDGE,"E12.3.0"),sQuery(id+"F8.wireOp",EDGE,"E12.3.1"),sQuery(id+"F8.wireOp",EDGE,"E12.4.0"),sQuery(id+"F8.wireOp",EDGE,"E12.4.1"),sQuery(id+"F8.wireOp",EDGE,"E12.5.0"),sQuery(id+"F8.wireOp",EDGE,"E12.5.1"),sQuery(id+"F8.wireOp",EDGE,"E12.6.0"),sQuery(id+"F8.wireOp",EDGE,"E13"),sQuery(id+"F8.wireOp",EDGE,"E14")])]}),"instanceName":"2"}),"instanceName":"1"});
            var Q3;
            Q3=makeQuery(id+"F3.opExtrude","SWEPT_BODY",BODY,{"disambiguationData":[OSD([sQuery(id+"F1.wireOp",EDGE,"E2.0"),sQuery(id+"F1.wireOp",EDGE,"E2.1"),sQuery(id+"F1.wireOp",EDGE,"E2.2"),sQuery(id+"F1.wireOp",EDGE,"E2.3"),sQuery(id+"F1.wireOp",EDGE,"E2.4"),sQuery(id+"F1.wireOp",EDGE,"E2.5")])]});
            var Q4;
            Q4=sQuery(id+"F51.wireOp",EDGE,"E52");
            circularPattern(context, id + "F52", {"entities" : qUnion([Q0, Q1, Q2, Q3]), "axis" : qUnion([Q4]), "angle" : 120 * degree, "instanceCount" : round(2), "oppositeDirection" : true});
        }
        {
            var Q0;
            Q0=makeQuery(id+"F32.opPattern","COPY",FACE,{"derivedFrom":makeQuery(id+"F26.opPattern","COPY",FACE,{"derivedFrom":makeQuery(id+"F3.opExtrude","CAP_FACE",FACE,{"disambiguationData":[OSD([sQuery(id+"F1.wireOp",EDGE,"E2.0"),sQuery(id+"F1.wireOp",EDGE,"E2.1"),sQuery(id+"F1.wireOp",EDGE,"E2.2"),sQuery(id+"F1.wireOp",EDGE,"E2.3"),sQuery(id+"F1.wireOp",EDGE,"E2.4"),sQuery(id+"F1.wireOp",EDGE,"E2.5")])],"isStart":true}),"instanceName":"2"}),"instanceName":"1"});
            var sketch = newSketch(context, id + "F53", { "sketchPlane" : qUnion([Q0])});
            skLineSegment(sketch, "E53", {"start": v(-10.6, -33.35) * mm, "end": v(-10.6, -18.35) * mm});
            skSolve(sketch);
        }
        {
            var Q0;
            Q0=sQuery(id+"F53.wireOp",VERTEX,"E53.start");
            var Q1;
            Q1=sQuery(id+"F53.wireOp",VERTEX,"E53.end");
            var Q2;
            Q2=makeQuery(id+"F32.opPattern","COPY",VERTEX,{"derivedFrom":makeQuery(id+"F26.opPattern","COPY",VERTEX,{"derivedFrom":makeQuery(id+"F3.opExtrude","CAP_VERTEX",VERTEX,{"disambiguationData":[OSD([sQuery(id+"F1.wireOp",EDGE,"E2.2"),sQuery(id+"F1.wireOp",EDGE,"E2.3")])],"isStart":false}),"instanceName":"2"}),"instanceName":"1"});
            cPlane(context, id + "F54", {"entities" : qUnion([Q0, Q1, Q2]), "cplaneType" : CPlaneType.THREE_POINT, "offset" : 150 * mm, "width" : 150 * mm, "height" : 150 * mm});
        }
        {
            var Q0;
            Q0=qCreatedBy(id+"F54.planeOp",FACE);
            var sketch = newSketch(context, id + "F55", { "sketchPlane" : qUnion([Q0])});
            skLineSegment(sketch, "E54.0", {"start": v(-2, -70.16) * mm, "end": v(-14.98, -62.66) * mm});
            skLineSegment(sketch, "E55", {"start": v(-14.98, -62.66) * mm, "end": v(-37.7, -102) * mm});
            skSolve(sketch);
        }
        {
            var Q0;
            Q0=makeQuery(id+"F26.opPattern","COPY",BODY,{"derivedFrom":makeQuery(id+"F3.opExtrude","SWEPT_BODY",BODY,{"disambiguationData":[OSD([sQuery(id+"F1.wireOp",EDGE,"E2.0"),sQuery(id+"F1.wireOp",EDGE,"E2.1"),sQuery(id+"F1.wireOp",EDGE,"E2.2"),sQuery(id+"F1.wireOp",EDGE,"E2.3"),sQuery(id+"F1.wireOp",EDGE,"E2.4"),sQuery(id+"F1.wireOp",EDGE,"E2.5")])]}),"instanceName":"2"});
            var Q1;
            Q1=makeQuery(id+"F26.opPattern","COPY",BODY,{"derivedFrom":makeQuery(id+"F16.opPattern","COPY",BODY,{"derivedFrom":makeQuery(id+"F15.opPattern","COPY",BODY,{"derivedFrom":makeQuery(id+"F9.opExtrude","SWEPT_BODY",BODY,{"disambiguationData":[OSD([sQuery(id+"F8.wireOp",EDGE,"E7.0"),sQuery(id+"F8.wireOp",EDGE,"E10"),sQuery(id+"F8.wireOp",EDGE,"E11"),sQuery(id+"F8.wireOp",EDGE,"E12.1.0"),sQuery(id+"F8.wireOp",EDGE,"E12.1.1"),sQuery(id+"F8.wireOp",EDGE,"E12.2.0"),sQuery(id+"F8.wireOp",EDGE,"E12.2.1"),sQuery(id+"F8.wireOp",EDGE,"E12.3.0"),sQuery(id+"F8.wireOp",EDGE,"E12.3.1"),sQuery(id+"F8.wireOp",EDGE,"E12.4.0"),sQuery(id+"F8.wireOp",EDGE,"E12.4.1"),sQuery(id+"F8.wireOp",EDGE,"E12.5.0"),sQuery(id+"F8.wireOp",EDGE,"E12.5.1"),sQuery(id+"F8.wireOp",EDGE,"E12.6.0"),sQuery(id+"F8.wireOp",EDGE,"E13"),sQuery(id+"F8.wireOp",EDGE,"E14")])]}),"instanceName":"2"}),"instanceName":"1"}),"instanceName":"2"});
            var Q2;
            Q2=makeQuery(id+"F26.opPattern","COPY",BODY,{"derivedFrom":makeQuery(id+"F13.opPattern","COPY",BODY,{"derivedFrom":makeQuery(id+"F9.opExtrude","SWEPT_BODY",BODY,{"disambiguationData":[OSD([sQuery(id+"F8.wireOp",EDGE,"E7.0"),sQuery(id+"F8.wireOp",EDGE,"E10"),sQuery(id+"F8.wireOp",EDGE,"E11"),sQuery(id+"F8.wireOp",EDGE,"E12.1.0"),sQuery(id+"F8.wireOp",EDGE,"E12.1.1"),sQuery(id+"F8.wireOp",EDGE,"E12.2.0"),sQuery(id+"F8.wireOp",EDGE,"E12.2.1"),sQuery(id+"F8.wireOp",EDGE,"E12.3.0"),sQuery(id+"F8.wireOp",EDGE,"E12.3.1"),sQuery(id+"F8.wireOp",EDGE,"E12.4.0"),sQuery(id+"F8.wireOp",EDGE,"E12.4.1"),sQuery(id+"F8.wireOp",EDGE,"E12.5.0"),sQuery(id+"F8.wireOp",EDGE,"E12.5.1"),sQuery(id+"F8.wireOp",EDGE,"E12.6.0"),sQuery(id+"F8.wireOp",EDGE,"E13"),sQuery(id+"F8.wireOp",EDGE,"E14")])]}),"instanceName":"1"}),"instanceName":"2"});
            var Q3;
            Q3=makeQuery(id+"F18.opPattern","COPY",BODY,{"derivedFrom":makeQuery(id+"F13.opPattern","COPY",BODY,{"derivedFrom":makeQuery(id+"F9.opExtrude","SWEPT_BODY",BODY,{"disambiguationData":[OSD([sQuery(id+"F8.wireOp",EDGE,"E7.0"),sQuery(id+"F8.wireOp",EDGE,"E10"),sQuery(id+"F8.wireOp",EDGE,"E11"),sQuery(id+"F8.wireOp",EDGE,"E12.1.0"),sQuery(id+"F8.wireOp",EDGE,"E12.1.1"),sQuery(id+"F8.wireOp",EDGE,"E12.2.0"),sQuery(id+"F8.wireOp",EDGE,"E12.2.1"),sQuery(id+"F8.wireOp",EDGE,"E12.3.0"),sQuery(id+"F8.wireOp",EDGE,"E12.3.1"),sQuery(id+"F8.wireOp",EDGE,"E12.4.0"),sQuery(id+"F8.wireOp",EDGE,"E12.4.1"),sQuery(id+"F8.wireOp",EDGE,"E12.5.0"),sQuery(id+"F8.wireOp",EDGE,"E12.5.1"),sQuery(id+"F8.wireOp",EDGE,"E12.6.0"),sQuery(id+"F8.wireOp",EDGE,"E13"),sQuery(id+"F8.wireOp",EDGE,"E14")])]}),"instanceName":"2"}),"instanceName":"2"});
            var Q4;
            Q4=sQuery(id+"F55.wireOp",EDGE,"E55");
            circularPattern(context, id + "F56", {"entities" : qUnion([Q0, Q1, Q2, Q3]), "axis" : qUnion([Q4]), "angle" : 120 * degree, "instanceCount" : 2, "oppositeDirection" : true});
        }
        {
            var Q0;
            Q0=makeQuery(id+"F56.opPattern","COPY",FACE,{"derivedFrom":makeQuery(id+"F26.opPattern","COPY",FACE,{"derivedFrom":makeQuery(id+"F3.opExtrude","CAP_FACE",FACE,{"disambiguationData":[OSD([sQuery(id+"F1.wireOp",EDGE,"E2.0"),sQuery(id+"F1.wireOp",EDGE,"E2.1"),sQuery(id+"F1.wireOp",EDGE,"E2.2"),sQuery(id+"F1.wireOp",EDGE,"E2.3"),sQuery(id+"F1.wireOp",EDGE,"E2.4"),sQuery(id+"F1.wireOp",EDGE,"E2.5")])],"isStart":true}),"instanceName":"2"}),"instanceName":"1"});
            var sketch = newSketch(context, id + "F57", { "sketchPlane" : qUnion([Q0])});
            skLineSegment(sketch, "E56", {"start": v(-34.48, 6) * mm, "end": v(-19.62, 8.02) * mm});
            skSolve(sketch);
        }
        {
            var Q0;
            Q0=sQuery(id+"F57.wireOp",VERTEX,"E56.start");
            var Q1;
            Q1=sQuery(id+"F57.wireOp",VERTEX,"E56.end");
            var Q2;
            Q2=makeQuery(id+"F56.opPattern","COPY",VERTEX,{"derivedFrom":makeQuery(id+"F26.opPattern","COPY",VERTEX,{"derivedFrom":makeQuery(id+"F3.opExtrude","CAP_VERTEX",VERTEX,{"disambiguationData":[OSD([sQuery(id+"F1.wireOp",EDGE,"E2.2"),sQuery(id+"F1.wireOp",EDGE,"E2.3")])],"isStart":false}),"instanceName":"2"}),"instanceName":"1"});
            cPlane(context, id + "F58", {"entities" : qUnion([Q0, Q1, Q2]), "cplaneType" : CPlaneType.THREE_POINT, "offset" : 150 * mm, "width" : 150 * mm, "height" : 150 * mm});
        }
        {
            var Q0;
            Q0=qCreatedBy(id+"F58.planeOp",FACE);
            var sketch = newSketch(context, id + "F59", { "sketchPlane" : qUnion([Q0])});
            skLineSegment(sketch, "E57.0", {"start": v(-8.72, -69.64) * mm, "end": v(-20.93, -60.93) * mm});
            skLineSegment(sketch, "E58", {"start": v(-20.93, -60.93) * mm, "end": v(-30.12, -73.8) * mm});
            skSolve(sketch);
        }
        {
            var Q0;
            Q0=makeQuery(id+"F52.opPattern","COPY",BODY,{"derivedFrom":makeQuery(id+"F3.opExtrude","SWEPT_BODY",BODY,{"disambiguationData":[OSD([sQuery(id+"F1.wireOp",EDGE,"E2.0"),sQuery(id+"F1.wireOp",EDGE,"E2.1"),sQuery(id+"F1.wireOp",EDGE,"E2.2"),sQuery(id+"F1.wireOp",EDGE,"E2.3"),sQuery(id+"F1.wireOp",EDGE,"E2.4"),sQuery(id+"F1.wireOp",EDGE,"E2.5")])]}),"instanceName":"1"});
            var Q1;
            Q1=makeQuery(id+"F52.opPattern","COPY",BODY,{"derivedFrom":makeQuery(id+"F16.opPattern","COPY",BODY,{"derivedFrom":makeQuery(id+"F15.opPattern","COPY",BODY,{"derivedFrom":makeQuery(id+"F9.opExtrude","SWEPT_BODY",BODY,{"disambiguationData":[OSD([sQuery(id+"F8.wireOp",EDGE,"E7.0"),sQuery(id+"F8.wireOp",EDGE,"E10"),sQuery(id+"F8.wireOp",EDGE,"E11"),sQuery(id+"F8.wireOp",EDGE,"E12.1.0"),sQuery(id+"F8.wireOp",EDGE,"E12.1.1"),sQuery(id+"F8.wireOp",EDGE,"E12.2.0"),sQuery(id+"F8.wireOp",EDGE,"E12.2.1"),sQuery(id+"F8.wireOp",EDGE,"E12.3.0"),sQuery(id+"F8.wireOp",EDGE,"E12.3.1"),sQuery(id+"F8.wireOp",EDGE,"E12.4.0"),sQuery(id+"F8.wireOp",EDGE,"E12.4.1"),sQuery(id+"F8.wireOp",EDGE,"E12.5.0"),sQuery(id+"F8.wireOp",EDGE,"E12.5.1"),sQuery(id+"F8.wireOp",EDGE,"E12.6.0"),sQuery(id+"F8.wireOp",EDGE,"E13"),sQuery(id+"F8.wireOp",EDGE,"E14")])]}),"instanceName":"2"}),"instanceName":"1"}),"instanceName":"1"});
            var Q2;
            Q2=makeQuery(id+"F52.opPattern","COPY",BODY,{"derivedFrom":makeQuery(id+"F16.opPattern","COPY",BODY,{"derivedFrom":makeQuery(id+"F15.opPattern","COPY",BODY,{"derivedFrom":makeQuery(id+"F9.opExtrude","SWEPT_BODY",BODY,{"disambiguationData":[OSD([sQuery(id+"F8.wireOp",EDGE,"E7.0"),sQuery(id+"F8.wireOp",EDGE,"E10"),sQuery(id+"F8.wireOp",EDGE,"E11"),sQuery(id+"F8.wireOp",EDGE,"E12.1.0"),sQuery(id+"F8.wireOp",EDGE,"E12.1.1"),sQuery(id+"F8.wireOp",EDGE,"E12.2.0"),sQuery(id+"F8.wireOp",EDGE,"E12.2.1"),sQuery(id+"F8.wireOp",EDGE,"E12.3.0"),sQuery(id+"F8.wireOp",EDGE,"E12.3.1"),sQuery(id+"F8.wireOp",EDGE,"E12.4.0"),sQuery(id+"F8.wireOp",EDGE,"E12.4.1"),sQuery(id+"F8.wireOp",EDGE,"E12.5.0"),sQuery(id+"F8.wireOp",EDGE,"E12.5.1"),sQuery(id+"F8.wireOp",EDGE,"E12.6.0"),sQuery(id+"F8.wireOp",EDGE,"E13"),sQuery(id+"F8.wireOp",EDGE,"E14")])]}),"instanceName":"1"}),"instanceName":"1"}),"instanceName":"1"});
            var Q3;
            Q3=makeQuery(id+"F52.opPattern","COPY",BODY,{"derivedFrom":makeQuery(id+"F13.opPattern","COPY",BODY,{"derivedFrom":makeQuery(id+"F9.opExtrude","SWEPT_BODY",BODY,{"disambiguationData":[OSD([sQuery(id+"F8.wireOp",EDGE,"E7.0"),sQuery(id+"F8.wireOp",EDGE,"E10"),sQuery(id+"F8.wireOp",EDGE,"E11"),sQuery(id+"F8.wireOp",EDGE,"E12.1.0"),sQuery(id+"F8.wireOp",EDGE,"E12.1.1"),sQuery(id+"F8.wireOp",EDGE,"E12.2.0"),sQuery(id+"F8.wireOp",EDGE,"E12.2.1"),sQuery(id+"F8.wireOp",EDGE,"E12.3.0"),sQuery(id+"F8.wireOp",EDGE,"E12.3.1"),sQuery(id+"F8.wireOp",EDGE,"E12.4.0"),sQuery(id+"F8.wireOp",EDGE,"E12.4.1"),sQuery(id+"F8.wireOp",EDGE,"E12.5.0"),sQuery(id+"F8.wireOp",EDGE,"E12.5.1"),sQuery(id+"F8.wireOp",EDGE,"E12.6.0"),sQuery(id+"F8.wireOp",EDGE,"E13"),sQuery(id+"F8.wireOp",EDGE,"E14")])]}),"instanceName":"1"}),"instanceName":"1"});
            var Q4;
            Q4=sQuery(id+"F59.wireOp",EDGE,"E58");
            circularPattern(context, id + "F60", {"entities" : qUnion([Q0, Q1, Q2, Q3]), "axis" : qUnion([Q4]), "angle" : 120 * degree, "instanceCount" : 2, "oppositeDirection" : true});
        }
        {
            var Q0;
            Q0=makeQuery(id+"F22.opPattern","COPY",BODY,{"derivedFrom":makeQuery(id+"F17.opPattern","COPY",BODY,{"derivedFrom":makeQuery(id+"F16.opPattern","COPY",BODY,{"derivedFrom":makeQuery(id+"F15.opPattern","COPY",BODY,{"derivedFrom":makeQuery(id+"F9.opExtrude","SWEPT_BODY",BODY,{"disambiguationData":[OSD([sQuery(id+"F8.wireOp",EDGE,"E7.0"),sQuery(id+"F8.wireOp",EDGE,"E10"),sQuery(id+"F8.wireOp",EDGE,"E11"),sQuery(id+"F8.wireOp",EDGE,"E12.1.0"),sQuery(id+"F8.wireOp",EDGE,"E12.1.1"),sQuery(id+"F8.wireOp",EDGE,"E12.2.0"),sQuery(id+"F8.wireOp",EDGE,"E12.2.1"),sQuery(id+"F8.wireOp",EDGE,"E12.3.0"),sQuery(id+"F8.wireOp",EDGE,"E12.3.1"),sQuery(id+"F8.wireOp",EDGE,"E12.4.0"),sQuery(id+"F8.wireOp",EDGE,"E12.4.1"),sQuery(id+"F8.wireOp",EDGE,"E12.5.0"),sQuery(id+"F8.wireOp",EDGE,"E12.5.1"),sQuery(id+"F8.wireOp",EDGE,"E12.6.0"),sQuery(id+"F8.wireOp",EDGE,"E13"),sQuery(id+"F8.wireOp",EDGE,"E14")])]}),"instanceName":"1"}),"instanceName":"1"}),"instanceName":"1"}),"instanceName":"1"});
            deleteBodies(context, id + "F61", {"entities" : qUnion([Q0])});
        }
        {
            var Q0;
            Q0=makeQuery(id+"F22.opPattern","COPY",BODY,{"derivedFrom":makeQuery(id+"F17.opPattern","COPY",BODY,{"derivedFrom":makeQuery(id+"F16.opPattern","COPY",BODY,{"derivedFrom":makeQuery(id+"F15.opPattern","COPY",BODY,{"derivedFrom":makeQuery(id+"F9.opExtrude","SWEPT_BODY",BODY,{"disambiguationData":[OSD([sQuery(id+"F8.wireOp",EDGE,"E7.0"),sQuery(id+"F8.wireOp",EDGE,"E10"),sQuery(id+"F8.wireOp",EDGE,"E11"),sQuery(id+"F8.wireOp",EDGE,"E12.1.0"),sQuery(id+"F8.wireOp",EDGE,"E12.1.1"),sQuery(id+"F8.wireOp",EDGE,"E12.2.0"),sQuery(id+"F8.wireOp",EDGE,"E12.2.1"),sQuery(id+"F8.wireOp",EDGE,"E12.3.0"),sQuery(id+"F8.wireOp",EDGE,"E12.3.1"),sQuery(id+"F8.wireOp",EDGE,"E12.4.0"),sQuery(id+"F8.wireOp",EDGE,"E12.4.1"),sQuery(id+"F8.wireOp",EDGE,"E12.5.0"),sQuery(id+"F8.wireOp",EDGE,"E12.5.1"),sQuery(id+"F8.wireOp",EDGE,"E12.6.0"),sQuery(id+"F8.wireOp",EDGE,"E13"),sQuery(id+"F8.wireOp",EDGE,"E14")])]}),"instanceName":"1"}),"instanceName":"1"}),"instanceName":"1"}),"instanceName":"2"});
            deleteBodies(context, id + "F62", {"entities" : qUnion([Q0])});
        }
        {
            var Q0;
            Q0=makeQuery(id+"F26.opPattern","COPY",BODY,{"derivedFrom":makeQuery(id+"F16.opPattern","COPY",BODY,{"derivedFrom":makeQuery(id+"F15.opPattern","COPY",BODY,{"derivedFrom":makeQuery(id+"F9.opExtrude","SWEPT_BODY",BODY,{"disambiguationData":[OSD([sQuery(id+"F8.wireOp",EDGE,"E7.0"),sQuery(id+"F8.wireOp",EDGE,"E10"),sQuery(id+"F8.wireOp",EDGE,"E11"),sQuery(id+"F8.wireOp",EDGE,"E12.1.0"),sQuery(id+"F8.wireOp",EDGE,"E12.1.1"),sQuery(id+"F8.wireOp",EDGE,"E12.2.0"),sQuery(id+"F8.wireOp",EDGE,"E12.2.1"),sQuery(id+"F8.wireOp",EDGE,"E12.3.0"),sQuery(id+"F8.wireOp",EDGE,"E12.3.1"),sQuery(id+"F8.wireOp",EDGE,"E12.4.0"),sQuery(id+"F8.wireOp",EDGE,"E12.4.1"),sQuery(id+"F8.wireOp",EDGE,"E12.5.0"),sQuery(id+"F8.wireOp",EDGE,"E12.5.1"),sQuery(id+"F8.wireOp",EDGE,"E12.6.0"),sQuery(id+"F8.wireOp",EDGE,"E13"),sQuery(id+"F8.wireOp",EDGE,"E14")])]}),"instanceName":"1"}),"instanceName":"1"}),"instanceName":"1"});
            deleteBodies(context, id + "F63", {"entities" : qUnion([Q0])});
        }
        {
            var Q0;
            Q0=makeQuery(id+"F26.opPattern","COPY",BODY,{"derivedFrom":makeQuery(id+"F16.opPattern","COPY",BODY,{"derivedFrom":makeQuery(id+"F15.opPattern","COPY",BODY,{"derivedFrom":makeQuery(id+"F9.opExtrude","SWEPT_BODY",BODY,{"disambiguationData":[OSD([sQuery(id+"F8.wireOp",EDGE,"E7.0"),sQuery(id+"F8.wireOp",EDGE,"E10"),sQuery(id+"F8.wireOp",EDGE,"E11"),sQuery(id+"F8.wireOp",EDGE,"E12.1.0"),sQuery(id+"F8.wireOp",EDGE,"E12.1.1"),sQuery(id+"F8.wireOp",EDGE,"E12.2.0"),sQuery(id+"F8.wireOp",EDGE,"E12.2.1"),sQuery(id+"F8.wireOp",EDGE,"E12.3.0"),sQuery(id+"F8.wireOp",EDGE,"E12.3.1"),sQuery(id+"F8.wireOp",EDGE,"E12.4.0"),sQuery(id+"F8.wireOp",EDGE,"E12.4.1"),sQuery(id+"F8.wireOp",EDGE,"E12.5.0"),sQuery(id+"F8.wireOp",EDGE,"E12.5.1"),sQuery(id+"F8.wireOp",EDGE,"E12.6.0"),sQuery(id+"F8.wireOp",EDGE,"E13"),sQuery(id+"F8.wireOp",EDGE,"E14")])]}),"instanceName":"1"}),"instanceName":"1"}),"instanceName":"2"});
            deleteBodies(context, id + "F64", {"entities" : qUnion([Q0])});
        }
        {
            var Q0;
            Q0=qCreatedBy(makeId("Top.planeOp"),FACE);
            var sketch = newSketch(context, id + "F65", { "sketchPlane" : qUnion([Q0])});
            skCircle(sketch, "E59", {"center": v(0, 0) * mm, "radius": 5 * mm});
            skSolve(sketch);
        }
        {
            var Q0;
            Q0 = qSketchRegion(id + "F65", true);
            extrude(context, id + "F66", {"entities" : qUnion([Q0]), "operationType" : NewBodyOperationType.ADD, "depth" : 1000 * mm, "offsetDistance" : 25 * mm});
        }
        {
            var Q0;
            Q0 = qSketchRegion(id + "F65", true);
            extrude(context, id + "F67", {"entities" : qUnion([Q0]), "operationType" : NewBodyOperationType.ADD, "oppositeDirection" : true, "depth" : 25 * mm, "offsetDistance" : 25 * mm});
        }
    });
